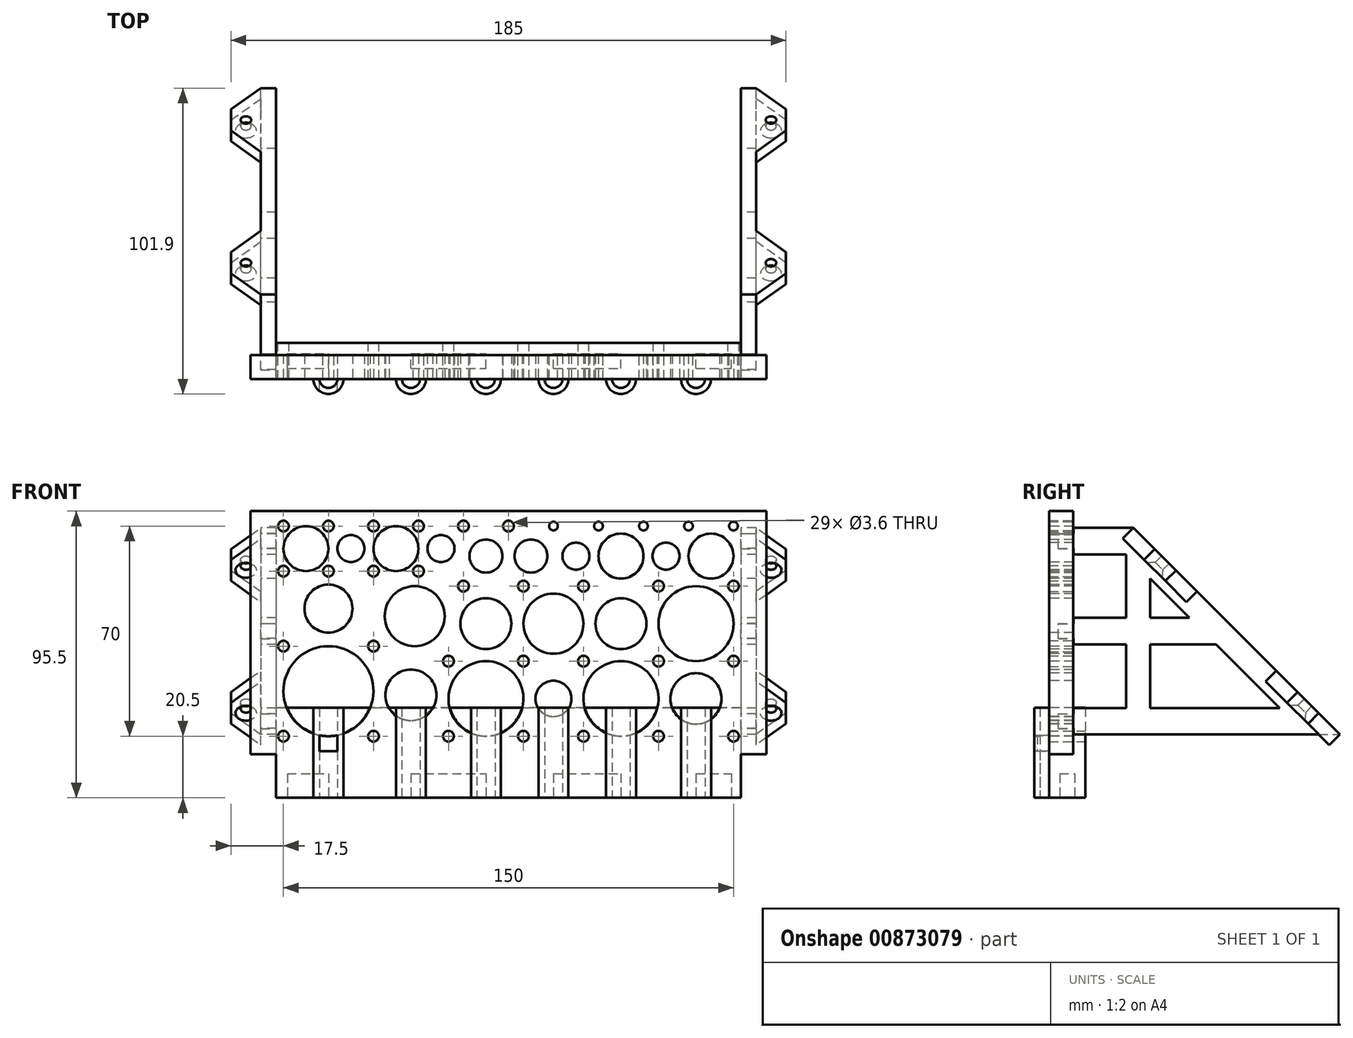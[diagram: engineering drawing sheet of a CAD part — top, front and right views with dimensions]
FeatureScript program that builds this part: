
annotation { "Feature Type Name" : "Feature", "Feature Type Description" : "" }
export const myFeature = defineFeature(function(context is Context, id is Id, definition is map)
    precondition{}
    {
        {
            var Q0;
            Q0=qCreatedBy(makeId("Front.planeOp"),FACE);
            var sketch = newSketch(context, id + "F0", { "sketchPlane" : qUnion([Q0])});
            skCircle(sketch, "E0", {"center": v(-34.8, 20.35) * mm, "radius": 1.8 * mm});
            skCircle(sketch, "E1.0.1.0", {"center": v(-34.8, 50.35) * mm, "radius": 1.8 * mm});
            skCircle(sketch, "E1.1.0.0", {"center": v(-4.8, 20.35) * mm, "radius": 1.8 * mm});
            skCircle(sketch, "E1.1.1.0", {"center": v(-4.8, 50.35) * mm, "radius": 1.8 * mm});
            skLineSegment(sketch, "E1.direction1", {"start": v(-34.8, 20.35) * mm, "end": v(-4.8, 20.35) * mm, "construction": true});
            skLineSegment(sketch, "E1.direction2", {"start": v(-34.8, 20.35) * mm, "end": v(-34.8, 50.35) * mm, "construction": true});
            skCircle(sketch, "E2", {"center": v(20.2, 20.35) * mm, "radius": 1.8 * mm});
            skCircle(sketch, "E3.0.1.0", {"center": v(20.2, 45.35) * mm, "radius": 1.8 * mm});
            skCircle(sketch, "E3.1.0.0", {"center": v(45.2, 20.35) * mm, "radius": 1.8 * mm});
            skCircle(sketch, "E3.1.1.0", {"center": v(45.2, 45.35) * mm, "radius": 1.8 * mm});
            skLineSegment(sketch, "E3.direction1", {"start": v(20.2, 20.35) * mm, "end": v(45.2, 20.35) * mm, "construction": true});
            skLineSegment(sketch, "E3.direction2", {"start": v(20.2, 20.35) * mm, "end": v(20.2, 45.35) * mm, "construction": true});
            skCircle(sketch, "E4", {"center": v(65.2, 20.35) * mm, "radius": 1.8 * mm});
            skCircle(sketch, "E5.0.1.0", {"center": v(65.2, 45.35) * mm, "radius": 1.8 * mm});
            skCircle(sketch, "E5.0.2.0", {"center": v(65.2, 70.35) * mm, "radius": 1.8 * mm});
            skCircle(sketch, "E5.1.0.0", {"center": v(90.2, 20.35) * mm, "radius": 1.8 * mm});
            skCircle(sketch, "E5.1.1.0", {"center": v(90.2, 45.35) * mm, "radius": 1.8 * mm});
            skCircle(sketch, "E5.1.2.0", {"center": v(90.2, 70.35) * mm, "radius": 1.8 * mm});
            skCircle(sketch, "E5.2.0.0", {"center": v(115.2, 20.35) * mm, "radius": 1.8 * mm});
            skCircle(sketch, "E5.2.1.0", {"center": v(115.2, 45.35) * mm, "radius": 1.8 * mm});
            skCircle(sketch, "E5.2.2.0", {"center": v(115.2, 70.35) * mm, "radius": 1.8 * mm});
            skLineSegment(sketch, "E5.direction1", {"start": v(65.2, 20.35) * mm, "end": v(90.2, 20.35) * mm, "construction": true});
            skLineSegment(sketch, "E5.direction2", {"start": v(65.2, 20.35) * mm, "end": v(65.2, 45.35) * mm, "construction": true});
            skCircle(sketch, "E6", {"center": v(-34.8, 90.35) * mm, "radius": 1.8 * mm});
            skCircle(sketch, "E7.1.0.0", {"center": v(-19.8, 90.35) * mm, "radius": 1.8 * mm});
            skCircle(sketch, "E7.2.0.0", {"center": v(-4.8, 90.35) * mm, "radius": 1.8 * mm});
            skCircle(sketch, "E7.3.0.0", {"center": v(10.2, 90.35) * mm, "radius": 1.8 * mm});
            skCircle(sketch, "E7.4.0.0", {"center": v(25.2, 90.35) * mm, "radius": 1.8 * mm});
            skCircle(sketch, "E7.5.0.0", {"center": v(40.2, 90.35) * mm, "radius": 1.8 * mm});
            skLineSegment(sketch, "E7.direction1", {"start": v(-34.8, 90.35) * mm, "end": v(-19.8, 90.35) * mm, "construction": true});
            skCircle(sketch, "E8.0.6.0", {"center": v(55.2, 90.35) * mm, "radius": 1.45 * mm});
            skCircle(sketch, "E8.0.7.0", {"center": v(70.2, 90.35) * mm, "radius": 1.45 * mm});
            skCircle(sketch, "E8.0.8.0", {"center": v(85.2, 90.35) * mm, "radius": 1.45 * mm});
            skCircle(sketch, "E8.0.9.0", {"center": v(100.2, 90.35) * mm, "radius": 1.45 * mm});
            skCircle(sketch, "E9.0.10.0", {"center": v(115.2, 90.35) * mm, "radius": 1.45 * mm});
            skCircle(sketch, "E10.1.0.0", {"center": v(45.2, 70.35) * mm, "radius": 1.8 * mm});
            skCircle(sketch, "E10.2.0.0", {"center": v(25.2, 70.35) * mm, "radius": 1.8 * mm});
            skLineSegment(sketch, "E10.direction1", {"start": v(65.2, 70.35) * mm, "end": v(45.2, 70.35) * mm, "construction": true});
            skLineSegment(sketch, "E11", {"start": v(-39.8, 95.35) * mm, "end": v(-39.8, 15.35) * mm, "construction": true});
            skLineSegment(sketch, "E12", {"start": v(120.2, 95.35) * mm, "end": v(120.2, 15.35) * mm, "construction": true});
            skLineSegment(sketch, "E13", {"start": v(-39.8, 95.35) * mm, "end": v(120.2, 95.35) * mm});
            skLineSegment(sketch, "E14", {"start": v(120.2, 15.35) * mm, "end": v(-39.8, 15.35) * mm});
            skLineSegment(sketch, "E15", {"start": v(-39.8, 95.35) * mm, "end": v(-45.8, 95.35) * mm});
            skLineSegment(sketch, "E16", {"start": v(-39.8, 15.35) * mm, "end": v(-39.8, 15.35) * mm});
            skLineSegment(sketch, "E17", {"start": v(-39.8, 15.35) * mm, "end": v(-45.8, 15.35) * mm});
            skLineSegment(sketch, "E18", {"start": v(-45.8, 15.35) * mm, "end": v(-45.8, 95.35) * mm});
            skLineSegment(sketch, "E19", {"start": v(120.2, 95.35) * mm, "end": v(126.2, 95.35) * mm});
            skLineSegment(sketch, "E20", {"start": v(126.2, 95.35) * mm, "end": v(126.2, 15.35) * mm});
            skLineSegment(sketch, "E21", {"start": v(126.2, 15.35) * mm, "end": v(120.2, 15.35) * mm});
            skCircle(sketch, "E22", {"center": v(-34.8, 75.35) * mm, "radius": 1.8 * mm});
            skCircle(sketch, "E23.1.0.0", {"center": v(-19.8, 75.35) * mm, "radius": 1.8 * mm});
            skCircle(sketch, "E23.2.0.0", {"center": v(-4.8, 75.35) * mm, "radius": 1.8 * mm});
            skCircle(sketch, "E23.3.0.0", {"center": v(10.2, 75.35) * mm, "radius": 1.8 * mm});
            skLineSegment(sketch, "E23.direction1", {"start": v(-34.8, 75.35) * mm, "end": v(-19.8, 75.35) * mm, "construction": true});
            skSolve(sketch);
        }
        {
            var Q0;
            Q0=makeQuery(id+"F0.imprint","IMPRINT",FACE,{"disambiguationData":[TD([[makeQuery(id+"F0.imprint","IMPRINT",EDGE,{"derivedFrom":sQuery(id+"F0.wireOp",EDGE,"E0")}),-1.0]])]});
            extrude(context, id + "F1", {"entities" : qUnion([Q0]), "depth" : 8 * mm, "offsetDistance" : 25 * mm});
        }
        {
            var Q0;
            Q0=makeQuery(id+"F1.opExtrude","CAP_FACE",FACE,{"disambiguationData":[OSD([sQuery(id+"F0.wireOp",EDGE,"E0"),sQuery(id+"F0.wireOp",EDGE,"E1.0.1.0"),sQuery(id+"F0.wireOp",EDGE,"E1.1.0.0"),sQuery(id+"F0.wireOp",EDGE,"E1.1.1.0"),sQuery(id+"F0.wireOp",EDGE,"E2"),sQuery(id+"F0.wireOp",EDGE,"E3.0.1.0"),sQuery(id+"F0.wireOp",EDGE,"E3.1.0.0"),sQuery(id+"F0.wireOp",EDGE,"E3.1.1.0"),sQuery(id+"F0.wireOp",EDGE,"E4"),sQuery(id+"F0.wireOp",EDGE,"E5.0.1.0"),sQuery(id+"F0.wireOp",EDGE,"E5.0.2.0"),sQuery(id+"F0.wireOp",EDGE,"E5.1.0.0"),sQuery(id+"F0.wireOp",EDGE,"E5.1.1.0"),sQuery(id+"F0.wireOp",EDGE,"E5.1.2.0"),sQuery(id+"F0.wireOp",EDGE,"E5.2.0.0"),sQuery(id+"F0.wireOp",EDGE,"E5.2.1.0"),sQuery(id+"F0.wireOp",EDGE,"E5.2.2.0"),sQuery(id+"F0.wireOp",EDGE,"E6"),sQuery(id+"F0.wireOp",EDGE,"E7.1.0.0"),sQuery(id+"F0.wireOp",EDGE,"E7.2.0.0"),sQuery(id+"F0.wireOp",EDGE,"E7.3.0.0"),sQuery(id+"F0.wireOp",EDGE,"E7.4.0.0"),sQuery(id+"F0.wireOp",EDGE,"E7.5.0.0"),sQuery(id+"F0.wireOp",EDGE,"E8.0.6.0"),sQuery(id+"F0.wireOp",EDGE,"E8.0.7.0"),sQuery(id+"F0.wireOp",EDGE,"E8.0.8.0"),sQuery(id+"F0.wireOp",EDGE,"E8.0.9.0"),sQuery(id+"F0.wireOp",EDGE,"E9.0.10.0"),sQuery(id+"F0.wireOp",EDGE,"E10.1.0.0"),sQuery(id+"F0.wireOp",EDGE,"E10.2.0.0"),sQuery(id+"F0.wireOp",EDGE,"E13"),sQuery(id+"F0.wireOp",EDGE,"E14"),sQuery(id+"F0.wireOp",EDGE,"E15"),sQuery(id+"F0.wireOp",EDGE,"E17"),sQuery(id+"F0.wireOp",EDGE,"E18"),sQuery(id+"F0.wireOp",EDGE,"E19"),sQuery(id+"F0.wireOp",EDGE,"E20"),sQuery(id+"F0.wireOp",EDGE,"E21"),sQuery(id+"F0.wireOp",EDGE,"E22"),sQuery(id+"F0.wireOp",EDGE,"E23.1.0.0"),sQuery(id+"F0.wireOp",EDGE,"E23.2.0.0"),sQuery(id+"F0.wireOp",EDGE,"E23.3.0.0")])],"isStart":false});
            var sketch = newSketch(context, id + "F2", { "sketchPlane" : qUnion([Q0])});
            skLineSegment(sketch, "E24.0", {"start": v(126.2, 95.35) * mm, "end": v(126.2, 15.35) * mm});
            skLineSegment(sketch, "E24.1", {"start": v(-45.8, 95.35) * mm, "end": v(126.2, 95.35) * mm});
            skLineSegment(sketch, "E24.2", {"start": v(126.2, 15.35) * mm, "end": v(-45.8, 15.35) * mm});
            skLineSegment(sketch, "E24.3", {"start": v(-45.8, 15.35) * mm, "end": v(-45.8, 95.35) * mm});
            skLineSegment(sketch, "E25", {"start": v(-34.8, 50.35) * mm, "end": v(-4.8, 50.35) * mm, "construction": true});
            skLineSegment(sketch, "E26", {"start": v(-4.8, 50.35) * mm, "end": v(-4.8, 20.35) * mm, "construction": true});
            skLineSegment(sketch, "E27", {"start": v(-4.8, 20.35) * mm, "end": v(-34.8, 20.35) * mm, "construction": true});
            skLineSegment(sketch, "E28", {"start": v(-34.8, 20.35) * mm, "end": v(-34.8, 50.35) * mm, "construction": true});
            skLineSegment(sketch, "E29", {"start": v(20.2, 45.35) * mm, "end": v(45.2, 45.35) * mm, "construction": true});
            skLineSegment(sketch, "E30", {"start": v(45.2, 45.35) * mm, "end": v(45.2, 20.35) * mm, "construction": true});
            skLineSegment(sketch, "E31", {"start": v(45.2, 20.35) * mm, "end": v(20.2, 20.35) * mm, "construction": true});
            skLineSegment(sketch, "E32", {"start": v(20.2, 20.35) * mm, "end": v(20.2, 45.35) * mm, "construction": true});
            skLineSegment(sketch, "E33", {"start": v(45.2, 45.35) * mm, "end": v(115.2, 45.35) * mm, "construction": true});
            skLineSegment(sketch, "E34", {"start": v(45.2, 20.35) * mm, "end": v(115.2, 20.35) * mm, "construction": true});
            skLineSegment(sketch, "E35", {"start": v(65.2, 45.35) * mm, "end": v(65.2, 20.35) * mm, "construction": true});
            skLineSegment(sketch, "E36", {"start": v(90.2, 45.35) * mm, "end": v(90.2, 20.35) * mm, "construction": true});
            skLineSegment(sketch, "E37", {"start": v(115.2, 45.35) * mm, "end": v(115.2, 20.35) * mm, "construction": true});
            skCircle(sketch, "E38", {"center": v(-19.8, 35.35) * mm, "radius": 15 * mm});
            skPoint(sketch, "E38.centerSnap0", {"position": v(-19.8, 50.35) * mm});
            skPoint(sketch, "E38.centerSnap1", {"position": v(-34.8, 35.35) * mm});
            skCircle(sketch, "E39", {"center": v(32.7, 32.85) * mm, "radius": 12.5 * mm});
            skPoint(sketch, "E39.centerSnap0", {"position": v(32.7, 45.35) * mm});
            skPoint(sketch, "E39.centerSnap1", {"position": v(20.2, 32.85) * mm});
            skPoint(sketch, "E40", {"position": v(55.2, 32.85) * mm});
            skPoint(sketch, "E40.positionSnap0", {"position": v(65.2, 32.85) * mm});
            skPoint(sketch, "E41", {"position": v(77.7, 32.85) * mm});
            skPoint(sketch, "E42", {"position": v(102.7, 32.85) * mm});
            skCircle(sketch, "E43", {"center": v(55.2, 32.85) * mm, "radius": 6 * mm});
            skCircle(sketch, "E44", {"center": v(77.7, 32.85) * mm, "radius": 12.5 * mm});
            skCircle(sketch, "E45", {"center": v(102.7, 32.85) * mm, "radius": 8.5 * mm});
            skLineSegment(sketch, "E46", {"start": v(-19.8, 35.35) * mm, "end": v(32.7, 32.85) * mm, "construction": true});
            skPoint(sketch, "E47", {"position": v(7.7, 34.04) * mm});
            skCircle(sketch, "E48", {"center": v(7.7, 34.04) * mm, "radius": 8.5 * mm});
            skLineSegment(sketch, "E49", {"start": v(115.2, 90.35) * mm, "end": v(100.2, 90.35) * mm, "construction": true});
            skLineSegment(sketch, "E50", {"start": v(100.2, 90.35) * mm, "end": v(85.2, 90.35) * mm, "construction": true});
            skLineSegment(sketch, "E51", {"start": v(85.2, 90.35) * mm, "end": v(70.2, 90.35) * mm, "construction": true});
            skLineSegment(sketch, "E52", {"start": v(70.2, 90.35) * mm, "end": v(55.2, 90.35) * mm, "construction": true});
            skLineSegment(sketch, "E53", {"start": v(55.2, 90.35) * mm, "end": v(40.2, 90.35) * mm, "construction": true});
            skLineSegment(sketch, "E54", {"start": v(40.2, 90.35) * mm, "end": v(25.2, 90.35) * mm, "construction": true});
            skLineSegment(sketch, "E55", {"start": v(25.2, 90.35) * mm, "end": v(10.2, 90.35) * mm, "construction": true});
            skLineSegment(sketch, "E56", {"start": v(10.2, 90.35) * mm, "end": v(-4.8, 90.35) * mm, "construction": true});
            skLineSegment(sketch, "E57", {"start": v(-4.8, 90.35) * mm, "end": v(-19.8, 90.35) * mm, "construction": true});
            skLineSegment(sketch, "E58", {"start": v(-19.8, 90.35) * mm, "end": v(-34.8, 90.35) * mm, "construction": true});
            skLineSegment(sketch, "E59", {"start": v(-34.8, 90.35) * mm, "end": v(-34.8, 75.35) * mm, "construction": true});
            skCircle(sketch, "E60", {"center": v(-27.3, 82.85) * mm, "radius": 7.5 * mm});
            skPoint(sketch, "E60.centerSnap0", {"position": v(-27.3, 90.35) * mm});
            skPoint(sketch, "E60.centerSnap1", {"position": v(-34.8, 82.85) * mm});
            skCircle(sketch, "E61", {"center": v(2.7, 82.85) * mm, "radius": 7.5 * mm});
            skPoint(sketch, "E61.centerSnap0", {"position": v(2.7, 90.35) * mm});
            skCircle(sketch, "E62", {"center": v(-12.3, 82.85) * mm, "radius": 4.5 * mm});
            skPoint(sketch, "E62.centerSnap0", {"position": v(-12.3, 90.35) * mm});
            skCircle(sketch, "E63", {"center": v(17.7, 82.85) * mm, "radius": 4.5 * mm});
            skPoint(sketch, "E63.centerSnap0", {"position": v(17.7, 90.35) * mm});
            skLineSegment(sketch, "E64", {"start": v(-34.8, 75.35) * mm, "end": v(-34.8, 50.35) * mm, "construction": true});
            skLineSegment(sketch, "E65", {"start": v(-34.8, 62.85) * mm, "end": v(-4.8, 62.85) * mm, "construction": true});
            skLineSegment(sketch, "E66", {"start": v(20.2, 45.35) * mm, "end": v(25.2, 70.35) * mm, "construction": true});
            skLineSegment(sketch, "E67", {"start": v(22.7, 57.85) * mm, "end": v(-4.8, 62.85) * mm, "construction": true});
            skCircle(sketch, "E68", {"center": v(-19.8, 62.85) * mm, "radius": 8 * mm});
            skCircle(sketch, "E69", {"center": v(8.95, 60.35) * mm, "radius": 10 * mm});
            skLineSegment(sketch, "E70", {"start": v(25.2, 70.35) * mm, "end": v(45.2, 70.35) * mm, "construction": true});
            skLineSegment(sketch, "E71", {"start": v(45.2, 70.35) * mm, "end": v(65.2, 70.35) * mm, "construction": true});
            skLineSegment(sketch, "E72", {"start": v(65.2, 70.35) * mm, "end": v(90.2, 70.35) * mm, "construction": true});
            skLineSegment(sketch, "E73", {"start": v(90.2, 70.35) * mm, "end": v(115.2, 70.35) * mm, "construction": true});
            skLineSegment(sketch, "E74", {"start": v(115.2, 70.35) * mm, "end": v(115.2, 45.35) * mm, "construction": true});
            skLineSegment(sketch, "E75", {"start": v(115.2, 57.85) * mm, "end": v(22.7, 57.85) * mm, "construction": true});
            skCircle(sketch, "E76", {"center": v(102.7, 57.85) * mm, "radius": 12.5 * mm});
            skPoint(sketch, "E76.centerSnap0", {"position": v(102.7, 70.35) * mm});
            skCircle(sketch, "E77", {"center": v(77.7, 57.85) * mm, "radius": 8.5 * mm});
            skPoint(sketch, "E77.centerSnap0", {"position": v(77.7, 70.35) * mm});
            skCircle(sketch, "E78", {"center": v(55.2, 57.85) * mm, "radius": 10 * mm});
            skPoint(sketch, "E78.centerSnap0", {"position": v(55.2, 70.35) * mm});
            skCircle(sketch, "E79", {"center": v(32.68, 57.85) * mm, "radius": 8.5 * mm});
            skLineSegment(sketch, "E80", {"start": v(115.2, 90.35) * mm, "end": v(115.2, 70.35) * mm, "construction": true});
            skLineSegment(sketch, "E81", {"start": v(115.2, 80.35) * mm, "end": v(32.7, 80.35) * mm, "construction": true});
            skPoint(sketch, "E81.endSnap0", {"position": v(32.7, 90.35) * mm});
            skCircle(sketch, "E82", {"center": v(107.7, 80.35) * mm, "radius": 7.5 * mm});
            skPoint(sketch, "E82.centerSnap0", {"position": v(107.7, 90.35) * mm});
            skCircle(sketch, "E83", {"center": v(92.7, 80.35) * mm, "radius": 4.5 * mm});
            skPoint(sketch, "E83.centerSnap0", {"position": v(92.7, 90.35) * mm});
            skCircle(sketch, "E84", {"center": v(77.7, 80.35) * mm, "radius": 7.5 * mm});
            skPoint(sketch, "E84.centerSnap0", {"position": v(77.7, 90.35) * mm});
            skCircle(sketch, "E85", {"center": v(62.7, 80.35) * mm, "radius": 4.5 * mm});
            skPoint(sketch, "E85.centerSnap0", {"position": v(62.7, 90.35) * mm});
            skCircle(sketch, "E86", {"center": v(47.7, 80.35) * mm, "radius": 5.5 * mm});
            skPoint(sketch, "E86.centerSnap0", {"position": v(47.7, 90.35) * mm});
            skCircle(sketch, "E87", {"center": v(32.7, 80.35) * mm, "radius": 5.5 * mm});
            skSolve(sketch);
        }
        {
            var Q0;
            Q0=makeQuery(id+"F2.imprint","IMPRINT",FACE,{"disambiguationData":[TD([[makeQuery(id+"F2.imprint","IMPRINT",EDGE,{"derivedFrom":sQuery(id+"F2.wireOp",EDGE,"E45")}),1.0]])]});
            var Q1;
            Q1=makeQuery(id+"F2.imprint","IMPRINT",FACE,{"disambiguationData":[TD([[makeQuery(id+"F2.imprint","IMPRINT",EDGE,{"derivedFrom":sQuery(id+"F2.wireOp",EDGE,"E44")}),1.0]])]});
            var Q2;
            Q2=makeQuery(id+"F2.imprint","IMPRINT",FACE,{"disambiguationData":[TD([[makeQuery(id+"F2.imprint","IMPRINT",EDGE,{"derivedFrom":sQuery(id+"F2.wireOp",EDGE,"E43")}),1.0]])]});
            var Q3;
            Q3=makeQuery(id+"F2.imprint","IMPRINT",FACE,{"disambiguationData":[TD([[makeQuery(id+"F2.imprint","IMPRINT",EDGE,{"derivedFrom":sQuery(id+"F2.wireOp",EDGE,"E39")}),1.0]])]});
            var Q4;
            Q4=makeQuery(id+"F2.imprint","IMPRINT",FACE,{"disambiguationData":[TD([[makeQuery(id+"F2.imprint","IMPRINT",EDGE,{"derivedFrom":sQuery(id+"F2.wireOp",EDGE,"E48")}),1.0]])]});
            var Q5;
            Q5=makeQuery(id+"F2.imprint","IMPRINT",FACE,{"disambiguationData":[TD([[makeQuery(id+"F2.imprint","IMPRINT",EDGE,{"derivedFrom":sQuery(id+"F2.wireOp",EDGE,"E38")}),1.0]])]});
            var Q6;
            Q6=makeQuery(id+"F2.imprint","IMPRINT",FACE,{"disambiguationData":[TD([[makeQuery(id+"F2.imprint","IMPRINT",EDGE,{"derivedFrom":sQuery(id+"F2.wireOp",EDGE,"E68")}),1.0]])]});
            var Q7;
            Q7=makeQuery(id+"F2.imprint","IMPRINT",FACE,{"disambiguationData":[TD([[makeQuery(id+"F2.imprint","IMPRINT",EDGE,{"derivedFrom":sQuery(id+"F2.wireOp",EDGE,"E60")}),1.0]])]});
            var Q8;
            Q8=makeQuery(id+"F2.imprint","IMPRINT",FACE,{"disambiguationData":[TD([[makeQuery(id+"F2.imprint","IMPRINT",EDGE,{"derivedFrom":sQuery(id+"F2.wireOp",EDGE,"E62")}),1.0]])]});
            var Q9;
            Q9=makeQuery(id+"F2.imprint","IMPRINT",FACE,{"disambiguationData":[TD([[makeQuery(id+"F2.imprint","IMPRINT",EDGE,{"derivedFrom":sQuery(id+"F2.wireOp",EDGE,"E61")}),1.0]])]});
            var Q10;
            Q10=makeQuery(id+"F2.imprint","IMPRINT",FACE,{"disambiguationData":[TD([[makeQuery(id+"F2.imprint","IMPRINT",EDGE,{"derivedFrom":sQuery(id+"F2.wireOp",EDGE,"E63")}),1.0]])]});
            var Q11;
            Q11=makeQuery(id+"F2.imprint","IMPRINT",FACE,{"disambiguationData":[TD([[makeQuery(id+"F2.imprint","IMPRINT",EDGE,{"derivedFrom":sQuery(id+"F2.wireOp",EDGE,"E69")}),1.0]])]});
            var Q12;
            Q12=makeQuery(id+"F2.imprint","IMPRINT",FACE,{"disambiguationData":[TD([[makeQuery(id+"F2.imprint","IMPRINT",EDGE,{"derivedFrom":sQuery(id+"F2.wireOp",EDGE,"E79")}),1.0]])]});
            var Q13;
            Q13=makeQuery(id+"F2.imprint","IMPRINT",FACE,{"disambiguationData":[TD([[makeQuery(id+"F2.imprint","IMPRINT",EDGE,{"derivedFrom":sQuery(id+"F2.wireOp",EDGE,"E78")}),1.0]])]});
            var Q14;
            Q14=makeQuery(id+"F2.imprint","IMPRINT",FACE,{"disambiguationData":[TD([[makeQuery(id+"F2.imprint","IMPRINT",EDGE,{"derivedFrom":sQuery(id+"F2.wireOp",EDGE,"E77")}),1.0]])]});
            var Q15;
            Q15=makeQuery(id+"F2.imprint","IMPRINT",FACE,{"disambiguationData":[TD([[makeQuery(id+"F2.imprint","IMPRINT",EDGE,{"derivedFrom":sQuery(id+"F2.wireOp",EDGE,"E76")}),1.0]])]});
            var Q16;
            Q16=makeQuery(id+"F2.imprint","IMPRINT",FACE,{"disambiguationData":[TD([[makeQuery(id+"F2.imprint","IMPRINT",EDGE,{"derivedFrom":sQuery(id+"F2.wireOp",EDGE,"E87")}),1.0]])]});
            var Q17;
            Q17=makeQuery(id+"F2.imprint","IMPRINT",FACE,{"disambiguationData":[TD([[makeQuery(id+"F2.imprint","IMPRINT",EDGE,{"derivedFrom":sQuery(id+"F2.wireOp",EDGE,"E86")}),1.0]])]});
            var Q18;
            Q18=makeQuery(id+"F2.imprint","IMPRINT",FACE,{"disambiguationData":[TD([[makeQuery(id+"F2.imprint","IMPRINT",EDGE,{"derivedFrom":sQuery(id+"F2.wireOp",EDGE,"E85")}),1.0]])]});
            var Q19;
            Q19=makeQuery(id+"F2.imprint","IMPRINT",FACE,{"disambiguationData":[TD([[makeQuery(id+"F2.imprint","IMPRINT",EDGE,{"derivedFrom":sQuery(id+"F2.wireOp",EDGE,"E84")}),1.0]])]});
            var Q20;
            Q20=makeQuery(id+"F2.imprint","IMPRINT",FACE,{"disambiguationData":[TD([[makeQuery(id+"F2.imprint","IMPRINT",EDGE,{"derivedFrom":sQuery(id+"F2.wireOp",EDGE,"E83")}),1.0]])]});
            var Q21;
            Q21=makeQuery(id+"F2.imprint","IMPRINT",FACE,{"disambiguationData":[TD([[makeQuery(id+"F2.imprint","IMPRINT",EDGE,{"derivedFrom":sQuery(id+"F2.wireOp",EDGE,"E82")}),1.0]])]});
            extrude(context, id + "F3", {"entities" : qUnion([Q0, Q1, Q2, Q3, Q4, Q5, Q6, Q7, Q8, Q9, Q10, Q11, Q12, Q13, Q14, Q15, Q16, Q17, Q18, Q19, Q20, Q21]), "operationType" : NewBodyOperationType.REMOVE, "oppositeDirection" : true, "depth" : 8 * mm, "offsetDistance" : 25 * mm});
        }
        {
            var Q0;
            Q0=makeQuery(id+"F1.opExtrude","CAP_FACE",FACE,{"disambiguationData":[OSD([sQuery(id+"F0.wireOp",EDGE,"E0"),sQuery(id+"F0.wireOp",EDGE,"E1.0.1.0"),sQuery(id+"F0.wireOp",EDGE,"E1.1.0.0"),sQuery(id+"F0.wireOp",EDGE,"E1.1.1.0"),sQuery(id+"F0.wireOp",EDGE,"E2"),sQuery(id+"F0.wireOp",EDGE,"E3.0.1.0"),sQuery(id+"F0.wireOp",EDGE,"E3.1.0.0"),sQuery(id+"F0.wireOp",EDGE,"E3.1.1.0"),sQuery(id+"F0.wireOp",EDGE,"E4"),sQuery(id+"F0.wireOp",EDGE,"E5.0.1.0"),sQuery(id+"F0.wireOp",EDGE,"E5.0.2.0"),sQuery(id+"F0.wireOp",EDGE,"E5.1.0.0"),sQuery(id+"F0.wireOp",EDGE,"E5.1.1.0"),sQuery(id+"F0.wireOp",EDGE,"E5.1.2.0"),sQuery(id+"F0.wireOp",EDGE,"E5.2.0.0"),sQuery(id+"F0.wireOp",EDGE,"E5.2.1.0"),sQuery(id+"F0.wireOp",EDGE,"E5.2.2.0"),sQuery(id+"F0.wireOp",EDGE,"E6"),sQuery(id+"F0.wireOp",EDGE,"E7.1.0.0"),sQuery(id+"F0.wireOp",EDGE,"E7.2.0.0"),sQuery(id+"F0.wireOp",EDGE,"E7.3.0.0"),sQuery(id+"F0.wireOp",EDGE,"E7.4.0.0"),sQuery(id+"F0.wireOp",EDGE,"E7.5.0.0"),sQuery(id+"F0.wireOp",EDGE,"E8.0.6.0"),sQuery(id+"F0.wireOp",EDGE,"E8.0.7.0"),sQuery(id+"F0.wireOp",EDGE,"E8.0.8.0"),sQuery(id+"F0.wireOp",EDGE,"E8.0.9.0"),sQuery(id+"F0.wireOp",EDGE,"E9.0.10.0"),sQuery(id+"F0.wireOp",EDGE,"E10.1.0.0"),sQuery(id+"F0.wireOp",EDGE,"E10.2.0.0"),sQuery(id+"F0.wireOp",EDGE,"E13"),sQuery(id+"F0.wireOp",EDGE,"E14"),sQuery(id+"F0.wireOp",EDGE,"E15"),sQuery(id+"F0.wireOp",EDGE,"E17"),sQuery(id+"F0.wireOp",EDGE,"E18"),sQuery(id+"F0.wireOp",EDGE,"E19"),sQuery(id+"F0.wireOp",EDGE,"E20"),sQuery(id+"F0.wireOp",EDGE,"E21"),sQuery(id+"F0.wireOp",EDGE,"E22"),sQuery(id+"F0.wireOp",EDGE,"E23.1.0.0"),sQuery(id+"F0.wireOp",EDGE,"E23.2.0.0"),sQuery(id+"F0.wireOp",EDGE,"E23.3.0.0")])],"isStart":true});
            var sketch = newSketch(context, id + "F4", { "sketchPlane" : qUnion([Q0])});
            skLineSegment(sketch, "E88.0", {"start": v(45.8, 95.35) * mm, "end": v(-126.2, 95.35) * mm});
            skLineSegment(sketch, "E88.1", {"start": v(45.8, 15.35) * mm, "end": v(45.8, 95.35) * mm});
            skLineSegment(sketch, "E88.2", {"start": v(-126.2, 15.35) * mm, "end": v(45.8, 15.35) * mm});
            skLineSegment(sketch, "E88.3", {"start": v(-126.2, 95.35) * mm, "end": v(-126.2, 15.35) * mm});
            skLineSegment(sketch, "E89.bottom", {"start": v(-117.7, 82.85) * mm, "end": v(-122.7, 82.85) * mm});
            skLineSegment(sketch, "E89.top", {"start": v(-117.7, 87.85) * mm, "end": v(-122.7, 87.85) * mm});
            skLineSegment(sketch, "E89.left", {"start": v(-117.7, 82.85) * mm, "end": v(-117.7, 87.85) * mm});
            skLineSegment(sketch, "E89.right", {"start": v(-122.7, 82.85) * mm, "end": v(-122.7, 87.85) * mm});
            skPoint(sketch, "E89.middle", {"position": v(-120.2, 85.35) * mm});
            skLineSegment(sketch, "E90.bottom", {"start": v(-122.7, 52.85) * mm, "end": v(-117.7, 52.85) * mm});
            skLineSegment(sketch, "E90.top", {"start": v(-122.7, 57.85) * mm, "end": v(-117.7, 57.85) * mm});
            skLineSegment(sketch, "E90.left", {"start": v(-122.7, 52.85) * mm, "end": v(-122.7, 57.85) * mm});
            skLineSegment(sketch, "E90.right", {"start": v(-117.7, 52.85) * mm, "end": v(-117.7, 57.85) * mm});
            skPoint(sketch, "E90.middle", {"position": v(-120.2, 55.35) * mm});
            skLineSegment(sketch, "E91.bottom", {"start": v(-122.7, 22.85) * mm, "end": v(-117.7, 22.85) * mm});
            skLineSegment(sketch, "E91.top", {"start": v(-122.7, 27.85) * mm, "end": v(-117.7, 27.85) * mm});
            skLineSegment(sketch, "E91.left", {"start": v(-122.7, 22.85) * mm, "end": v(-122.7, 27.85) * mm});
            skLineSegment(sketch, "E91.right", {"start": v(-117.7, 22.85) * mm, "end": v(-117.7, 27.85) * mm});
            skPoint(sketch, "E91.middle", {"position": v(-120.2, 25.35) * mm});
            skLineSegment(sketch, "E92", {"start": v(-40.2, 95.35) * mm, "end": v(-40.2, 15.35) * mm, "construction": true});
            skLineSegment(sketch, "E93.MirrorCS", {"start": v(37.3, 87.85) * mm, "end": v(42.3, 87.85) * mm});
            skLineSegment(sketch, "E94.MirrorCS", {"start": v(37.3, 82.85) * mm, "end": v(37.3, 87.85) * mm});
            skLineSegment(sketch, "E95.MirrorCS", {"start": v(37.3, 82.85) * mm, "end": v(42.3, 82.85) * mm});
            skLineSegment(sketch, "E96.MirrorCS", {"start": v(42.3, 82.85) * mm, "end": v(42.3, 87.85) * mm});
            skLineSegment(sketch, "E97.MirrorCS", {"start": v(42.3, 57.85) * mm, "end": v(37.3, 57.85) * mm});
            skLineSegment(sketch, "E98.MirrorCS", {"start": v(37.3, 52.85) * mm, "end": v(37.3, 57.85) * mm});
            skLineSegment(sketch, "E99.MirrorCS", {"start": v(42.3, 52.85) * mm, "end": v(37.3, 52.85) * mm});
            skLineSegment(sketch, "E100.MirrorCS", {"start": v(42.3, 52.85) * mm, "end": v(42.3, 57.85) * mm});
            skLineSegment(sketch, "E101.MirrorCS", {"start": v(42.3, 27.85) * mm, "end": v(37.3, 27.85) * mm});
            skLineSegment(sketch, "E102.MirrorCS", {"start": v(37.3, 22.85) * mm, "end": v(37.3, 27.85) * mm});
            skLineSegment(sketch, "E103.MirrorCS", {"start": v(42.3, 22.85) * mm, "end": v(37.3, 22.85) * mm});
            skLineSegment(sketch, "E104.MirrorCS", {"start": v(42.3, 22.85) * mm, "end": v(42.3, 27.85) * mm});
            skSolve(sketch);
        }
        {
            var Q0;
            Q0=makeQuery(id+"F4.imprint","IMPRINT",FACE,{"disambiguationData":[TD([[makeQuery(id+"F4.imprint","IMPRINT",EDGE,{"derivedFrom":sQuery(id+"F4.wireOp",EDGE,"E89.bottom")}),-1.0]])]});
            var Q1;
            Q1=makeQuery(id+"F4.imprint","IMPRINT",FACE,{"disambiguationData":[TD([[makeQuery(id+"F4.imprint","IMPRINT",EDGE,{"derivedFrom":sQuery(id+"F4.wireOp",EDGE,"E90.bottom")}),1.0]])]});
            var Q2;
            Q2=makeQuery(id+"F4.imprint","IMPRINT",FACE,{"disambiguationData":[TD([[makeQuery(id+"F4.imprint","IMPRINT",EDGE,{"derivedFrom":sQuery(id+"F4.wireOp",EDGE,"E91.bottom")}),1.0]])]});
            var Q3;
            Q3=makeQuery(id+"F4.imprint","IMPRINT",FACE,{"disambiguationData":[TD([[makeQuery(id+"F4.imprint","IMPRINT",EDGE,{"derivedFrom":sQuery(id+"F4.wireOp",EDGE,"E101.MirrorCS")}),1.0]])]});
            var Q4;
            Q4=makeQuery(id+"F4.imprint","IMPRINT",FACE,{"disambiguationData":[TD([[makeQuery(id+"F4.imprint","IMPRINT",EDGE,{"derivedFrom":sQuery(id+"F4.wireOp",EDGE,"E97.MirrorCS")}),1.0]])]});
            var Q5;
            Q5=makeQuery(id+"F4.imprint","IMPRINT",FACE,{"disambiguationData":[TD([[makeQuery(id+"F4.imprint","IMPRINT",EDGE,{"derivedFrom":sQuery(id+"F4.wireOp",EDGE,"E93.MirrorCS")}),-1.0]])]});
            extrude(context, id + "F5", {"entities" : qUnion([Q0, Q1, Q2, Q3, Q4, Q5]), "operationType" : NewBodyOperationType.REMOVE, "oppositeDirection" : true, "depth" : 5 * mm, "offsetDistance" : 25 * mm});
        }
        {
            var Q0;
            Q0=makeQuery(id+"F5.boolean.opBoolean","COPY",FACE,{"derivedFrom":makeQuery(id+"F5.opExtrude","SWEPT_FACE",FACE,{"disambiguationData":[OSD([sQuery(id+"F4.wireOp",EDGE,"E89.left")])]})});
            var sketch = newSketch(context, id + "F6", { "sketchPlane" : qUnion([Q0])});
            skLineSegment(sketch, "E105.0", {"start": v(-4.9, 87.75) * mm, "end": v(0, 87.75) * mm});
            skLineSegment(sketch, "E105.1", {"start": v(-4.9, 82.95) * mm, "end": v(-4.9, 87.75) * mm});
            skLineSegment(sketch, "E105.2", {"start": v(-4.9, 82.95) * mm, "end": v(0, 82.95) * mm});
            skLineSegment(sketch, "E106.0", {"start": v(-4.9, 57.75) * mm, "end": v(0, 57.75) * mm});
            skLineSegment(sketch, "E106.1", {"start": v(-4.9, 52.95) * mm, "end": v(-4.9, 57.75) * mm});
            skLineSegment(sketch, "E106.2", {"start": v(-4.9, 52.95) * mm, "end": v(0, 52.95) * mm});
            skLineSegment(sketch, "E107.0", {"start": v(-4.9, 27.75) * mm, "end": v(0, 27.75) * mm});
            skLineSegment(sketch, "E107.1", {"start": v(-4.9, 22.95) * mm, "end": v(-4.9, 27.75) * mm});
            skLineSegment(sketch, "E107.2", {"start": v(-4.9, 22.95) * mm, "end": v(0, 22.95) * mm});
            skLineSegment(sketch, "E108.0", {"start": v(0.1, 95.35) * mm, "end": v(0.1, 87.75) * mm});
            skLineSegment(sketch, "E109", {"start": v(0, 57.75) * mm, "end": v(0.1, 57.75) * mm});
            skLineSegment(sketch, "E110", {"start": v(0, 52.95) * mm, "end": v(0.1, 52.95) * mm});
            skLineSegment(sketch, "E111.trimOffspring", {"start": v(0.1, 52.95) * mm, "end": v(0.1, 27.75) * mm});
            skLineSegment(sketch, "E112", {"start": v(0.1, 59.75) * mm, "end": v(5.1, 59.75) * mm});
            skLineSegment(sketch, "E113", {"start": v(0.1, 50.95) * mm, "end": v(5.1, 50.95) * mm});
            skLineSegment(sketch, "E114", {"start": v(0, 87.75) * mm, "end": v(0.1, 87.75) * mm});
            skLineSegment(sketch, "E115", {"start": v(0, 82.95) * mm, "end": v(0.1, 82.95) * mm});
            skLineSegment(sketch, "E116.trimOffspring", {"start": v(0.1, 82.95) * mm, "end": v(0.1, 57.75) * mm});
            skLineSegment(sketch, "E117", {"start": v(0.1, 80.95) * mm, "end": v(5.1, 80.95) * mm});
            skLineSegment(sketch, "E118", {"start": v(0.1, 89.75) * mm, "end": v(5.1, 89.75) * mm});
            skLineSegment(sketch, "E119", {"start": v(0, 27.75) * mm, "end": v(0.1, 27.75) * mm});
            skLineSegment(sketch, "E120", {"start": v(0, 22.95) * mm, "end": v(0.1, 22.95) * mm});
            skLineSegment(sketch, "E121.trimOffspring", {"start": v(0.1, 22.95) * mm, "end": v(0.1, 15.35) * mm});
            skLineSegment(sketch, "E122", {"start": v(0.1, 29.75) * mm, "end": v(5.1, 29.75) * mm});
            skLineSegment(sketch, "E123", {"start": v(0.1, 20.95) * mm, "end": v(5.1, 20.95) * mm});
            skLineSegment(sketch, "E124", {"start": v(5.1, 89.75) * mm, "end": v(20.1, 89.75) * mm});
            skLineSegment(sketch, "E125", {"start": v(20.1, 89.75) * mm, "end": v(88.9, 20.95) * mm});
            skLineSegment(sketch, "E126", {"start": v(5.1, 20.95) * mm, "end": v(88.9, 20.95) * mm});
            skLineSegment(sketch, "E127", {"start": v(5.1, 29.75) * mm, "end": v(17.59, 29.75) * mm});
            skLineSegment(sketch, "E128", {"start": v(5.1, 50.95) * mm, "end": v(17.59, 50.95) * mm});
            skLineSegment(sketch, "E129", {"start": v(5.1, 59.75) * mm, "end": v(17.59, 59.75) * mm});
            skLineSegment(sketch, "E130", {"start": v(5.1, 80.95) * mm, "end": v(17.59, 80.95) * mm});
            skLineSegment(sketch, "E131.0", {"start": v(25.59, 72.95) * mm, "end": v(38.79, 59.75) * mm});
            skLineSegment(sketch, "E132.trimOffspring", {"start": v(47.59, 50.95) * mm, "end": v(68.79, 29.75) * mm});
            skLineSegment(sketch, "E133", {"start": v(17.59, 80.95) * mm, "end": v(17.59, 59.75) * mm});
            skLineSegment(sketch, "E134", {"start": v(25.59, 29.75) * mm, "end": v(25.59, 50.95) * mm});
            skLineSegment(sketch, "E135.trimOffspring", {"start": v(25.59, 59.75) * mm, "end": v(38.79, 59.75) * mm});
            skLineSegment(sketch, "E136.trimOffspring", {"start": v(25.59, 59.75) * mm, "end": v(25.59, 72.95) * mm});
            skLineSegment(sketch, "E137.trimOffspring", {"start": v(17.59, 50.95) * mm, "end": v(17.59, 29.75) * mm});
            skLineSegment(sketch, "E138.trimOffspring", {"start": v(25.59, 50.95) * mm, "end": v(47.59, 50.95) * mm});
            skLineSegment(sketch, "E139.trimOffspring", {"start": v(25.59, 29.75) * mm, "end": v(68.79, 29.75) * mm});
            skSolve(sketch);
        }
        {
            var Q0;
            Q0=makeQuery(id+"F6.imprint","IMPRINT",FACE,{"disambiguationData":[TD([[makeQuery(id+"F6.imprint","IMPRINT",EDGE,{"derivedFrom":sQuery(id+"F6.wireOp",EDGE,"E106.0")}),-1.0]])]});
            var Q1;
            {var subQ0=sQuery(id+"F6.wireOp",EDGE,"E105.0");Q1=makeQuery(id+"F6.imprint","IMPRINT",FACE,{"disambiguationData":[TD([[makeQuery(id+"F6.imprint","IMPRINT",EDGE,{"derivedFrom":subQ0}),-1.0]])]});}
            extrude(context, id + "F7", {"entities" : qUnion([Q0, Q1]), "depth" : 5 * mm, "offsetDistance" : 25 * mm});
        }
        {
            var Q0;
            Q0=makeQuery(id+"F7.opExtrude","SWEPT_BODY",BODY,{"disambiguationData":[OSD([sQuery(id+"F6.wireOp",EDGE,"E105.0"),sQuery(id+"F6.wireOp",EDGE,"E105.1"),sQuery(id+"F6.wireOp",EDGE,"E105.2"),sQuery(id+"F6.wireOp",EDGE,"E106.0"),sQuery(id+"F6.wireOp",EDGE,"E106.1"),sQuery(id+"F6.wireOp",EDGE,"E106.2"),sQuery(id+"F6.wireOp",EDGE,"E107.0"),sQuery(id+"F6.wireOp",EDGE,"E107.1"),sQuery(id+"F6.wireOp",EDGE,"E107.2"),sQuery(id+"F6.wireOp",EDGE,"E108.0"),sQuery(id+"F6.wireOp",EDGE,"E109"),sQuery(id+"F6.wireOp",EDGE,"E110"),sQuery(id+"F6.wireOp",EDGE,"E111.trimOffspring"),sQuery(id+"F6.wireOp",EDGE,"E112"),sQuery(id+"F6.wireOp",EDGE,"E113"),sQuery(id+"F6.wireOp",EDGE,"E114"),sQuery(id+"F6.wireOp",EDGE,"E115"),sQuery(id+"F6.wireOp",EDGE,"E116.trimOffspring"),sQuery(id+"F6.wireOp",EDGE,"E117"),sQuery(id+"F6.wireOp",EDGE,"E118"),sQuery(id+"F6.wireOp",EDGE,"E119"),sQuery(id+"F6.wireOp",EDGE,"E120"),sQuery(id+"F6.wireOp",EDGE,"E121.trimOffspring"),sQuery(id+"F6.wireOp",EDGE,"E122"),sQuery(id+"F6.wireOp",EDGE,"E123"),sQuery(id+"F6.wireOp",EDGE,"E124"),sQuery(id+"F6.wireOp",EDGE,"E125"),sQuery(id+"F6.wireOp",EDGE,"E126"),sQuery(id+"F6.wireOp",EDGE,"E127"),sQuery(id+"F6.wireOp",EDGE,"E128"),sQuery(id+"F6.wireOp",EDGE,"E129"),sQuery(id+"F6.wireOp",EDGE,"E130"),sQuery(id+"F6.wireOp",EDGE,"E131.0"),sQuery(id+"F6.wireOp",EDGE,"E132.trimOffspring"),sQuery(id+"F6.wireOp",EDGE,"E133"),sQuery(id+"F6.wireOp",EDGE,"E134"),sQuery(id+"F6.wireOp",EDGE,"E135.trimOffspring"),sQuery(id+"F6.wireOp",EDGE,"E136.trimOffspring"),sQuery(id+"F6.wireOp",EDGE,"E137.trimOffspring"),sQuery(id+"F6.wireOp",EDGE,"E138.trimOffspring"),sQuery(id+"F6.wireOp",EDGE,"E139.trimOffspring")])]});
            transform(context, id + "F8", {"entities" : qUnion([Q0]), "transformType" : TransformType.TRANSLATION_3D, "dx" : -160 * mm, "dy" : 0 * mm, "dz" : 0 * mm, "makeCopy" : true});
        }
        {
            var Q0;
            Q0=makeQuery(id+"F7.opExtrude","SWEPT_FACE",FACE,{"disambiguationData":[OSD([sQuery(id+"F6.wireOp",EDGE,"E125")])]});
            var sketch = newSketch(context, id + "F9", { "sketchPlane" : qUnion([Q0])});
            skLineSegment(sketch, "E140.0", {"start": v(-122.7, 49.25) * mm, "end": v(-117.7, 49.25) * mm});
            skLineSegment(sketch, "E140.1", {"start": v(-122.7, 49.25) * mm, "end": v(-122.7, -48.05) * mm});
            skLineSegment(sketch, "E140.2", {"start": v(-122.7, -48.05) * mm, "end": v(-117.7, -48.05) * mm});
            skLineSegment(sketch, "E141", {"start": v(-132.7, 39.25) * mm, "end": v(-132.7, 29.25) * mm});
            skLineSegment(sketch, "E142", {"start": v(-122.7, 0.6) * mm, "end": v(-117.7, 0.6) * mm, "construction": true});
            skLineSegment(sketch, "E143.MirrorCS", {"start": v(-132.7, -38.05) * mm, "end": v(-132.7, -28.05) * mm});
            skPoint(sketch, "E144", {"position": v(-127.7, 34.25) * mm});
            skPoint(sketch, "E145", {"position": v(-127.7, -33.05) * mm});
            skLineSegment(sketch, "E146", {"start": v(-132.7, 39.25) * mm, "end": v(-122.7, 49.25) * mm});
            skPoint(sketch, "E147", {"position": v(-122.7, 19.25) * mm});
            skLineSegment(sketch, "E148", {"start": v(-132.7, 29.25) * mm, "end": v(-122.7, 19.25) * mm});
            skPoint(sketch, "E149.orphan", {"position": v(-122.7, 39.25) * mm});
            skPoint(sketch, "E150.end.orphan", {"position": v(-122.7, 29.25) * mm});
            skLineSegment(sketch, "E151.MirrorCS", {"start": v(-132.7, -38.05) * mm, "end": v(-122.7, -48.05) * mm});
            skLineSegment(sketch, "E152.MirrorCS", {"start": v(-132.7, -28.05) * mm, "end": v(-122.7, -18.05) * mm});
            skPoint(sketch, "E153.orphan", {"position": v(-122.7, -28.05) * mm});
            skPoint(sketch, "E154.MirrorCS.start.orphan", {"position": v(-122.7, -38.05) * mm});
            skPoint(sketch, "E155", {"position": v(-122.7, 49.25) * mm});
            skPoint(sketch, "E156", {"position": v(-122.7, -48.05) * mm});
            skSolve(sketch);
        }
        {
            var Q0;
            Q0=makeQuery(id+"F8.opPattern","COPY",FACE,{"derivedFrom":makeQuery(id+"F7.opExtrude","SWEPT_FACE",FACE,{"disambiguationData":[OSD([sQuery(id+"F6.wireOp",EDGE,"E125")])]}),"instanceName":"1"});
            var sketch = newSketch(context, id + "F10", { "sketchPlane" : qUnion([Q0])});
            skLineSegment(sketch, "E157.0", {"start": v(42.3, -48.05) * mm, "end": v(37.3, -48.05) * mm});
            skLineSegment(sketch, "E157.1", {"start": v(42.3, -48.05) * mm, "end": v(42.3, 49.25) * mm});
            skLineSegment(sketch, "E157.2", {"start": v(42.3, 49.25) * mm, "end": v(37.3, 49.25) * mm});
            skLineSegment(sketch, "E158", {"start": v(52.3, -38.05) * mm, "end": v(52.3, -28.05) * mm});
            skLineSegment(sketch, "E159", {"start": v(42.3, 0.6) * mm, "end": v(37.3, 0.6) * mm, "construction": true});
            skLineSegment(sketch, "E160.MirrorCS", {"start": v(52.3, 39.25) * mm, "end": v(52.3, 29.25) * mm});
            skPoint(sketch, "E161", {"position": v(47.3, -33.05) * mm});
            skPoint(sketch, "E162", {"position": v(47.3, 34.25) * mm});
            skLineSegment(sketch, "E163", {"start": v(52.3, -38.05) * mm, "end": v(42.3, -48.05) * mm});
            skPoint(sketch, "E164", {"position": v(42.3, -18.05) * mm});
            skLineSegment(sketch, "E165", {"start": v(52.3, -28.05) * mm, "end": v(42.3, -18.05) * mm});
            skPoint(sketch, "E166.orphan", {"position": v(42.3, -38.05) * mm});
            skPoint(sketch, "E167.end.orphan", {"position": v(42.3, -28.05) * mm});
            skLineSegment(sketch, "E168.MirrorCS", {"start": v(52.3, 39.25) * mm, "end": v(42.3, 49.25) * mm});
            skLineSegment(sketch, "E169.MirrorCS", {"start": v(52.3, 29.25) * mm, "end": v(42.3, 19.25) * mm});
            skPoint(sketch, "E170.orphan", {"position": v(42.3, 29.25) * mm});
            skPoint(sketch, "E171.MirrorCS.start.orphan", {"position": v(42.3, 39.25) * mm});
            skPoint(sketch, "E172", {"position": v(42.3, -48.05) * mm});
            skPoint(sketch, "E173", {"position": v(42.3, 49.25) * mm});
            skSolve(sketch);
        }
        {
            var Q0;
            Q0=makeQuery(id+"F9.imprint","IMPRINT",FACE,{"disambiguationData":[TD([[makeQuery(id+"F9.imprint","IMPRINT",EDGE,{"derivedFrom":sQuery(id+"F9.wireOp",EDGE,"E141")}),1.0]])]});
            var Q1;
            Q1=makeQuery(id+"F9.imprint","IMPRINT",FACE,{"disambiguationData":[TD([[makeQuery(id+"F9.imprint","IMPRINT",EDGE,{"derivedFrom":sQuery(id+"F9.wireOp",EDGE,"E143.MirrorCS")}),-1.0]])]});
            extrude(context, id + "F11", {"entities" : qUnion([Q0, Q1]), "operationType" : NewBodyOperationType.ADD, "oppositeDirection" : true, "depth" : 5 * mm, "offsetDistance" : 25 * mm});
        }
        {
            var Q0;
            Q0=makeQuery(id+"F10.imprint","IMPRINT",FACE,{"disambiguationData":[TD([[makeQuery(id+"F10.imprint","IMPRINT",EDGE,{"derivedFrom":sQuery(id+"F10.wireOp",EDGE,"E160.MirrorCS")}),-1.0]])]});
            var Q1;
            Q1=makeQuery(id+"F10.imprint","IMPRINT",FACE,{"disambiguationData":[TD([[makeQuery(id+"F10.imprint","IMPRINT",EDGE,{"derivedFrom":sQuery(id+"F10.wireOp",EDGE,"E158")}),1.0]])]});
            extrude(context, id + "F12", {"entities" : qUnion([Q0, Q1]), "operationType" : NewBodyOperationType.ADD, "oppositeDirection" : true, "depth" : 5 * mm, "offsetDistance" : 25 * mm});
        }
        {
            var Q0;
            Q0=makeQuery(id+"F12.opExtrude","CAP_FACE",FACE,{"disambiguationData":[OSD([sQuery(id+"F10.wireOp",EDGE,"E157.1"),sQuery(id+"F10.wireOp",EDGE,"E160.MirrorCS"),sQuery(id+"F10.wireOp",EDGE,"E168.MirrorCS"),sQuery(id+"F10.wireOp",EDGE,"E169.MirrorCS")])],"isStart":false});
            var sketch = newSketch(context, id + "F13", { "sketchPlane" : qUnion([Q0])});
            skPoint(sketch, "E174.0", {"position": v(-47.3, 34.25) * mm});
            skPoint(sketch, "E174.1", {"position": v(-47.3, -33.05) * mm});
            skSolve(sketch);
        }
        {
            var Q0;
            Q0=sQuery(id+"F13.wireOp",VERTEX,"E174.0");
            var Q1;
            Q1=sQuery(id+"F13.wireOp",VERTEX,"E174.1");
            var Q2;
            Q2=makeQuery(id+"F8.opPattern","COPY",BODY,{"derivedFrom":makeQuery(id+"F7.opExtrude","SWEPT_BODY",BODY,{"disambiguationData":[OSD([sQuery(id+"F6.wireOp",EDGE,"E105.0"),sQuery(id+"F6.wireOp",EDGE,"E105.1"),sQuery(id+"F6.wireOp",EDGE,"E105.2"),sQuery(id+"F6.wireOp",EDGE,"E106.0"),sQuery(id+"F6.wireOp",EDGE,"E106.1"),sQuery(id+"F6.wireOp",EDGE,"E106.2"),sQuery(id+"F6.wireOp",EDGE,"E107.0"),sQuery(id+"F6.wireOp",EDGE,"E107.1"),sQuery(id+"F6.wireOp",EDGE,"E107.2"),sQuery(id+"F6.wireOp",EDGE,"E108.0"),sQuery(id+"F6.wireOp",EDGE,"E109"),sQuery(id+"F6.wireOp",EDGE,"E110"),sQuery(id+"F6.wireOp",EDGE,"E111.trimOffspring"),sQuery(id+"F6.wireOp",EDGE,"E112"),sQuery(id+"F6.wireOp",EDGE,"E113"),sQuery(id+"F6.wireOp",EDGE,"E114"),sQuery(id+"F6.wireOp",EDGE,"E115"),sQuery(id+"F6.wireOp",EDGE,"E116.trimOffspring"),sQuery(id+"F6.wireOp",EDGE,"E117"),sQuery(id+"F6.wireOp",EDGE,"E118"),sQuery(id+"F6.wireOp",EDGE,"E119"),sQuery(id+"F6.wireOp",EDGE,"E120"),sQuery(id+"F6.wireOp",EDGE,"E121.trimOffspring"),sQuery(id+"F6.wireOp",EDGE,"E122"),sQuery(id+"F6.wireOp",EDGE,"E123"),sQuery(id+"F6.wireOp",EDGE,"E124"),sQuery(id+"F6.wireOp",EDGE,"E125"),sQuery(id+"F6.wireOp",EDGE,"E126"),sQuery(id+"F6.wireOp",EDGE,"E127"),sQuery(id+"F6.wireOp",EDGE,"E128"),sQuery(id+"F6.wireOp",EDGE,"E129"),sQuery(id+"F6.wireOp",EDGE,"E130"),sQuery(id+"F6.wireOp",EDGE,"E131.0"),sQuery(id+"F6.wireOp",EDGE,"E132.trimOffspring"),sQuery(id+"F6.wireOp",EDGE,"E133"),sQuery(id+"F6.wireOp",EDGE,"E134"),sQuery(id+"F6.wireOp",EDGE,"E135.trimOffspring"),sQuery(id+"F6.wireOp",EDGE,"E136.trimOffspring"),sQuery(id+"F6.wireOp",EDGE,"E137.trimOffspring"),sQuery(id+"F6.wireOp",EDGE,"E138.trimOffspring"),sQuery(id+"F6.wireOp",EDGE,"E139.trimOffspring")])]}),"instanceName":"1"});
            hole(context, id + "F14", {"style" : HoleStyle.C_SINK, "endStyle" : HoleEndStyle.THROUGH, "holeDiameter" : 3.5 * mm, "cSinkDiameter" : 7 * mm, "cSinkAngle" : 82 * degree, "majorDiameter" : 5 * mm, "isTappedThrough" : true, "tappedDepth" : 12 * mm, "tapClearance" : 3, "locations" : qUnion([Q0, Q1]), "scope" : qUnion([Q2]), "startStyle" : HoleStartStyle.SKETCH});
        }
        {
            var Q0;
            Q0=makeQuery(id+"F11.opExtrude","CAP_FACE",FACE,{"disambiguationData":[OSD([sQuery(id+"F9.wireOp",EDGE,"E140.1"),sQuery(id+"F9.wireOp",EDGE,"E141"),sQuery(id+"F9.wireOp",EDGE,"E146"),sQuery(id+"F9.wireOp",EDGE,"E148")])],"isStart":false});
            var sketch = newSketch(context, id + "F15", { "sketchPlane" : qUnion([Q0])});
            skPoint(sketch, "E175.0", {"position": v(127.7, 34.25) * mm});
            skPoint(sketch, "E175.1", {"position": v(127.7, -33.05) * mm});
            skSolve(sketch);
        }
        {
            var Q0;
            Q0=sQuery(id+"F15.wireOp",VERTEX,"E175.0");
            var Q1;
            Q1=sQuery(id+"F15.wireOp",VERTEX,"E175.1");
            var Q2;
            Q2=makeQuery(id+"F7.opExtrude","SWEPT_BODY",BODY,{"disambiguationData":[OSD([sQuery(id+"F6.wireOp",EDGE,"E105.0"),sQuery(id+"F6.wireOp",EDGE,"E105.1"),sQuery(id+"F6.wireOp",EDGE,"E105.2"),sQuery(id+"F6.wireOp",EDGE,"E106.0"),sQuery(id+"F6.wireOp",EDGE,"E106.1"),sQuery(id+"F6.wireOp",EDGE,"E106.2"),sQuery(id+"F6.wireOp",EDGE,"E107.0"),sQuery(id+"F6.wireOp",EDGE,"E107.1"),sQuery(id+"F6.wireOp",EDGE,"E107.2"),sQuery(id+"F6.wireOp",EDGE,"E108.0"),sQuery(id+"F6.wireOp",EDGE,"E109"),sQuery(id+"F6.wireOp",EDGE,"E110"),sQuery(id+"F6.wireOp",EDGE,"E111.trimOffspring"),sQuery(id+"F6.wireOp",EDGE,"E112"),sQuery(id+"F6.wireOp",EDGE,"E113"),sQuery(id+"F6.wireOp",EDGE,"E114"),sQuery(id+"F6.wireOp",EDGE,"E115"),sQuery(id+"F6.wireOp",EDGE,"E116.trimOffspring"),sQuery(id+"F6.wireOp",EDGE,"E117"),sQuery(id+"F6.wireOp",EDGE,"E118"),sQuery(id+"F6.wireOp",EDGE,"E119"),sQuery(id+"F6.wireOp",EDGE,"E120"),sQuery(id+"F6.wireOp",EDGE,"E121.trimOffspring"),sQuery(id+"F6.wireOp",EDGE,"E122"),sQuery(id+"F6.wireOp",EDGE,"E123"),sQuery(id+"F6.wireOp",EDGE,"E124"),sQuery(id+"F6.wireOp",EDGE,"E125"),sQuery(id+"F6.wireOp",EDGE,"E126"),sQuery(id+"F6.wireOp",EDGE,"E127"),sQuery(id+"F6.wireOp",EDGE,"E128"),sQuery(id+"F6.wireOp",EDGE,"E129"),sQuery(id+"F6.wireOp",EDGE,"E130"),sQuery(id+"F6.wireOp",EDGE,"E131.0"),sQuery(id+"F6.wireOp",EDGE,"E132.trimOffspring"),sQuery(id+"F6.wireOp",EDGE,"E133"),sQuery(id+"F6.wireOp",EDGE,"E134"),sQuery(id+"F6.wireOp",EDGE,"E135.trimOffspring"),sQuery(id+"F6.wireOp",EDGE,"E136.trimOffspring"),sQuery(id+"F6.wireOp",EDGE,"E137.trimOffspring"),sQuery(id+"F6.wireOp",EDGE,"E138.trimOffspring"),sQuery(id+"F6.wireOp",EDGE,"E139.trimOffspring")])]});
            hole(context, id + "F16", {"style" : HoleStyle.C_SINK, "endStyle" : HoleEndStyle.THROUGH, "holeDiameter" : 3.5 * mm, "cSinkDiameter" : 7 * mm, "cSinkAngle" : 82 * degree, "majorDiameter" : 5 * mm, "isTappedThrough" : true, "tappedDepth" : 12 * mm, "tapClearance" : 3, "locations" : qUnion([Q0, Q1]), "scope" : qUnion([Q2]), "startStyle" : HoleStartStyle.SKETCH});
        }
        {
            var Q0;
            Q0=makeQuery(id+"F1.opExtrude","CAP_FACE",FACE,{"disambiguationData":[OSD([sQuery(id+"F0.wireOp",EDGE,"E0"),sQuery(id+"F0.wireOp",EDGE,"E1.0.1.0"),sQuery(id+"F0.wireOp",EDGE,"E1.1.0.0"),sQuery(id+"F0.wireOp",EDGE,"E1.1.1.0"),sQuery(id+"F0.wireOp",EDGE,"E2"),sQuery(id+"F0.wireOp",EDGE,"E3.0.1.0"),sQuery(id+"F0.wireOp",EDGE,"E3.1.0.0"),sQuery(id+"F0.wireOp",EDGE,"E3.1.1.0"),sQuery(id+"F0.wireOp",EDGE,"E4"),sQuery(id+"F0.wireOp",EDGE,"E5.0.1.0"),sQuery(id+"F0.wireOp",EDGE,"E5.0.2.0"),sQuery(id+"F0.wireOp",EDGE,"E5.1.0.0"),sQuery(id+"F0.wireOp",EDGE,"E5.1.1.0"),sQuery(id+"F0.wireOp",EDGE,"E5.1.2.0"),sQuery(id+"F0.wireOp",EDGE,"E5.2.0.0"),sQuery(id+"F0.wireOp",EDGE,"E5.2.1.0"),sQuery(id+"F0.wireOp",EDGE,"E5.2.2.0"),sQuery(id+"F0.wireOp",EDGE,"E6"),sQuery(id+"F0.wireOp",EDGE,"E7.1.0.0"),sQuery(id+"F0.wireOp",EDGE,"E7.2.0.0"),sQuery(id+"F0.wireOp",EDGE,"E7.3.0.0"),sQuery(id+"F0.wireOp",EDGE,"E7.4.0.0"),sQuery(id+"F0.wireOp",EDGE,"E7.5.0.0"),sQuery(id+"F0.wireOp",EDGE,"E8.0.6.0"),sQuery(id+"F0.wireOp",EDGE,"E8.0.7.0"),sQuery(id+"F0.wireOp",EDGE,"E8.0.8.0"),sQuery(id+"F0.wireOp",EDGE,"E8.0.9.0"),sQuery(id+"F0.wireOp",EDGE,"E9.0.10.0"),sQuery(id+"F0.wireOp",EDGE,"E10.1.0.0"),sQuery(id+"F0.wireOp",EDGE,"E10.2.0.0"),sQuery(id+"F0.wireOp",EDGE,"E13"),sQuery(id+"F0.wireOp",EDGE,"E14"),sQuery(id+"F0.wireOp",EDGE,"E15"),sQuery(id+"F0.wireOp",EDGE,"E17"),sQuery(id+"F0.wireOp",EDGE,"E18"),sQuery(id+"F0.wireOp",EDGE,"E19"),sQuery(id+"F0.wireOp",EDGE,"E20"),sQuery(id+"F0.wireOp",EDGE,"E21"),sQuery(id+"F0.wireOp",EDGE,"E22"),sQuery(id+"F0.wireOp",EDGE,"E23.1.0.0"),sQuery(id+"F0.wireOp",EDGE,"E23.2.0.0"),sQuery(id+"F0.wireOp",EDGE,"E23.3.0.0")])],"isStart":false});
            var sketch = newSketch(context, id + "F17", { "sketchPlane" : qUnion([Q0])});
            skLineSegment(sketch, "E176.1", {"start": v(126.2, 95.35) * mm, "end": v(126.2, 15.35) * mm});
            skLineSegment(sketch, "E176.2", {"start": v(-45.8, 15.35) * mm, "end": v(-45.8, 95.35) * mm});
            skArc(sketch, "E177.0", {"start": v(-33.64, 29.85) * mm, "mid": v(-19.8, 20.45) * mm, "end": v(-5.95, 29.85) * mm});
            skArc(sketch, "E178.0", {"start": v(0.42, 29.85) * mm, "mid": v(7.7, 25.64) * mm, "end": v(14.98, 29.85) * mm});
            skArc(sketch, "E179.0", {"start": v(20.67, 29.85) * mm, "mid": v(32.7, 20.45) * mm, "end": v(44.74, 29.85) * mm});
            skArc(sketch, "E180.0", {"start": v(50.12, 29.85) * mm, "mid": v(55.2, 26.95) * mm, "end": v(60.28, 29.85) * mm});
            skArc(sketch, "E181.0", {"start": v(65.67, 29.85) * mm, "mid": v(77.7, 20.45) * mm, "end": v(89.74, 29.85) * mm});
            skArc(sketch, "E182.0", {"start": v(94.86, 29.85) * mm, "mid": v(102.7, 24.45) * mm, "end": v(110.55, 29.85) * mm});
            skLineSegment(sketch, "E183.0", {"start": v(126.2, 14.85) * mm, "end": v(-45.8, 14.85) * mm});
            skLineSegment(sketch, "E184", {"start": v(-45.8, 29.85) * mm, "end": v(126.2, 29.85) * mm});
            skLineSegment(sketch, "E185", {"start": v(-37.3, -25.15) * mm, "end": v(117.7, -25.15) * mm});
            skLineSegment(sketch, "E186.0", {"start": v(-37.3, 29.85) * mm, "end": v(-37.3, 29.75) * mm});
            skLineSegment(sketch, "E186.1", {"start": v(117.7, 29.85) * mm, "end": v(117.7, 29.75) * mm});
            skLineSegment(sketch, "E187", {"start": v(-37.3, 29.75) * mm, "end": v(-37.3, -25.15) * mm});
            skLineSegment(sketch, "E188", {"start": v(117.7, 29.75) * mm, "end": v(117.7, -25.15) * mm});
            skPoint(sketch, "E189.orphan", {"position": v(-37.3, 50.95) * mm});
            skPoint(sketch, "E190.orphan", {"position": v(117.7, 50.95) * mm});
            skPoint(sketch, "E191.orphan", {"position": v(126.2, -25.15) * mm});
            skSolve(sketch);
        }
        {
            var Q0;
            {var subQ0=sQuery(id+"F17.wireOp",EDGE,"E177.0");Q0=makeQuery(id+"F17.imprint","IMPRINT",FACE,{"disambiguationData":[TD([[makeQuery(id+"F17.imprint","IMPRINT",EDGE,{"derivedFrom":subQ0}),1.0]])]});}
            var Q1;
            {var subQ0=sQuery(id+"F17.wireOp",EDGE,"E178.0");Q1=makeQuery(id+"F17.imprint","IMPRINT",FACE,{"disambiguationData":[TD([[makeQuery(id+"F17.imprint","IMPRINT",EDGE,{"derivedFrom":subQ0}),1.0]])]});}
            var Q2;
            {var subQ0=sQuery(id+"F17.wireOp",EDGE,"E179.0");Q2=makeQuery(id+"F17.imprint","IMPRINT",FACE,{"disambiguationData":[TD([[makeQuery(id+"F17.imprint","IMPRINT",EDGE,{"derivedFrom":subQ0}),1.0]])]});}
            var Q3;
            {var subQ0=sQuery(id+"F17.wireOp",EDGE,"E180.0");Q3=makeQuery(id+"F17.imprint","IMPRINT",FACE,{"disambiguationData":[TD([[makeQuery(id+"F17.imprint","IMPRINT",EDGE,{"derivedFrom":subQ0}),1.0]])]});}
            var Q4;
            {var subQ0=sQuery(id+"F17.wireOp",EDGE,"E181.0");Q4=makeQuery(id+"F17.imprint","IMPRINT",FACE,{"disambiguationData":[TD([[makeQuery(id+"F17.imprint","IMPRINT",EDGE,{"derivedFrom":subQ0}),1.0]])]});}
            var Q5;
            {var subQ0=sQuery(id+"F17.wireOp",EDGE,"E182.0");Q5=makeQuery(id+"F17.imprint","IMPRINT",FACE,{"disambiguationData":[TD([[makeQuery(id+"F17.imprint","IMPRINT",EDGE,{"derivedFrom":subQ0}),1.0]])]});}
            extrude(context, id + "F18", {"entities" : qUnion([Q0, Q1, Q2, Q3, Q4, Q5]), "oppositeDirection" : true, "depth" : 12 * mm, "offsetDistance" : 25 * mm});
        }
        {
            var Q0;
            Q0=makeQuery(id+"F1.opExtrude","CAP_FACE",FACE,{"disambiguationData":[OSD([sQuery(id+"F0.wireOp",EDGE,"E0"),sQuery(id+"F0.wireOp",EDGE,"E1.0.1.0"),sQuery(id+"F0.wireOp",EDGE,"E1.1.0.0"),sQuery(id+"F0.wireOp",EDGE,"E1.1.1.0"),sQuery(id+"F0.wireOp",EDGE,"E2"),sQuery(id+"F0.wireOp",EDGE,"E3.0.1.0"),sQuery(id+"F0.wireOp",EDGE,"E3.1.0.0"),sQuery(id+"F0.wireOp",EDGE,"E3.1.1.0"),sQuery(id+"F0.wireOp",EDGE,"E4"),sQuery(id+"F0.wireOp",EDGE,"E5.0.1.0"),sQuery(id+"F0.wireOp",EDGE,"E5.0.2.0"),sQuery(id+"F0.wireOp",EDGE,"E5.1.0.0"),sQuery(id+"F0.wireOp",EDGE,"E5.1.1.0"),sQuery(id+"F0.wireOp",EDGE,"E5.1.2.0"),sQuery(id+"F0.wireOp",EDGE,"E5.2.0.0"),sQuery(id+"F0.wireOp",EDGE,"E5.2.1.0"),sQuery(id+"F0.wireOp",EDGE,"E5.2.2.0"),sQuery(id+"F0.wireOp",EDGE,"E6"),sQuery(id+"F0.wireOp",EDGE,"E7.1.0.0"),sQuery(id+"F0.wireOp",EDGE,"E7.2.0.0"),sQuery(id+"F0.wireOp",EDGE,"E7.3.0.0"),sQuery(id+"F0.wireOp",EDGE,"E7.4.0.0"),sQuery(id+"F0.wireOp",EDGE,"E7.5.0.0"),sQuery(id+"F0.wireOp",EDGE,"E8.0.6.0"),sQuery(id+"F0.wireOp",EDGE,"E8.0.7.0"),sQuery(id+"F0.wireOp",EDGE,"E8.0.8.0"),sQuery(id+"F0.wireOp",EDGE,"E8.0.9.0"),sQuery(id+"F0.wireOp",EDGE,"E9.0.10.0"),sQuery(id+"F0.wireOp",EDGE,"E10.1.0.0"),sQuery(id+"F0.wireOp",EDGE,"E10.2.0.0"),sQuery(id+"F0.wireOp",EDGE,"E13"),sQuery(id+"F0.wireOp",EDGE,"E14"),sQuery(id+"F0.wireOp",EDGE,"E15"),sQuery(id+"F0.wireOp",EDGE,"E17"),sQuery(id+"F0.wireOp",EDGE,"E18"),sQuery(id+"F0.wireOp",EDGE,"E19"),sQuery(id+"F0.wireOp",EDGE,"E20"),sQuery(id+"F0.wireOp",EDGE,"E21"),sQuery(id+"F0.wireOp",EDGE,"E22"),sQuery(id+"F0.wireOp",EDGE,"E23.1.0.0"),sQuery(id+"F0.wireOp",EDGE,"E23.2.0.0"),sQuery(id+"F0.wireOp",EDGE,"E23.3.0.0")])],"isStart":true});
            var sketch = newSketch(context, id + "F19", { "sketchPlane" : qUnion([Q0])});
            skLineSegment(sketch, "E192.0", {"start": v(33.64, 29.85) * mm, "end": v(5.95, 29.85) * mm});
            skLineSegment(sketch, "E192.1", {"start": v(-126.2, 15.35) * mm, "end": v(45.8, 15.35) * mm});
            skLineSegment(sketch, "E192.2", {"start": v(37.3, 89.75) * mm, "end": v(37.3, 20.95) * mm});
            skLineSegment(sketch, "E192.3", {"start": v(-117.7, 89.75) * mm, "end": v(-117.7, 20.95) * mm});
            skLineSegment(sketch, "E193", {"start": v(5.95, 29.85) * mm, "end": v(-117.7, 29.85) * mm});
            skLineSegment(sketch, "E194", {"start": v(33.64, 29.85) * mm, "end": v(37.3, 29.85) * mm});
            skLineSegment(sketch, "E195", {"start": v(-117.7, 20.95) * mm, "end": v(-117.7, 15.35) * mm});
            skLineSegment(sketch, "E196", {"start": v(37.3, 20.95) * mm, "end": v(37.3, 15.35) * mm});
            skSolve(sketch);
        }
        {
            var Q0;
            Q0 = qSketchRegion(id + "F19", true);
            extrude(context, id + "F20", {"entities" : qUnion([Q0]), "operationType" : NewBodyOperationType.ADD, "depth" : 4 * mm, "offsetDistance" : 25 * mm});
        }
        {
            var Q0;
            Q0=makeQuery(id+"F20.opExtrude","SWEPT_FACE",FACE,{"disambiguationData":[OSD([sQuery(id+"F19.wireOp",EDGE,"E192.1")])]});
            extrude(context, id + "F21", {"entities" : qUnion([Q0]), "operationType" : NewBodyOperationType.ADD, "depth" : 1 * mm, "offsetDistance" : 25 * mm});
        }
        {
            var Q0;
            {var subQ5=sQuery(id+"F17.wireOp",EDGE,"E185");Q0=makeQuery(id+"F17.imprint","IMPRINT",FACE,{"disambiguationData":[TD([[makeQuery(id+"F17.imprint","IMPRINT",EDGE,{"derivedFrom":subQ5}),1.0]])]});}
            extrude(context, id + "F22", {"entities" : qUnion([Q0]), "operationType" : NewBodyOperationType.ADD, "oppositeDirection" : true, "depth" : 12 * mm, "offsetDistance" : 25 * mm});
        }
        {
            var Q0;
            Q0=makeQuery(id+"F17.imprint","IMPRINT",FACE,{"disambiguationData":[TD([[makeQuery(id+"F17.imprint","IMPRINT",EDGE,{"derivedFrom":makeQuery(id+"F1.opExtrude","CAP_EDGE",EDGE,{"disambiguationData":[OSD([sQuery(id+"F0.wireOp",EDGE,"E0")])],"isStart":false})}),1.0]])]});
            var Q1;
            Q1=makeQuery(id+"F17.imprint","IMPRINT",FACE,{"disambiguationData":[TD([[makeQuery(id+"F17.imprint","IMPRINT",EDGE,{"derivedFrom":makeQuery(id+"F1.opExtrude","CAP_EDGE",EDGE,{"disambiguationData":[OSD([sQuery(id+"F0.wireOp",EDGE,"E1.1.0.0")])],"isStart":false})}),1.0]])]});
            var Q2;
            Q2=makeQuery(id+"F17.imprint","IMPRINT",FACE,{"disambiguationData":[TD([[makeQuery(id+"F17.imprint","IMPRINT",EDGE,{"derivedFrom":makeQuery(id+"F1.opExtrude","CAP_EDGE",EDGE,{"disambiguationData":[OSD([sQuery(id+"F0.wireOp",EDGE,"E2")])],"isStart":false})}),1.0]])]});
            var Q3;
            Q3=makeQuery(id+"F17.imprint","IMPRINT",FACE,{"disambiguationData":[TD([[makeQuery(id+"F17.imprint","IMPRINT",EDGE,{"derivedFrom":makeQuery(id+"F1.opExtrude","CAP_EDGE",EDGE,{"disambiguationData":[OSD([sQuery(id+"F0.wireOp",EDGE,"E3.1.0.0")])],"isStart":false})}),1.0]])]});
            var Q4;
            Q4=makeQuery(id+"F17.imprint","IMPRINT",FACE,{"disambiguationData":[TD([[makeQuery(id+"F17.imprint","IMPRINT",EDGE,{"derivedFrom":makeQuery(id+"F1.opExtrude","CAP_EDGE",EDGE,{"disambiguationData":[OSD([sQuery(id+"F0.wireOp",EDGE,"E4")])],"isStart":false})}),1.0]])]});
            var Q5;
            Q5=makeQuery(id+"F17.imprint","IMPRINT",FACE,{"disambiguationData":[TD([[makeQuery(id+"F17.imprint","IMPRINT",EDGE,{"derivedFrom":makeQuery(id+"F1.opExtrude","CAP_EDGE",EDGE,{"disambiguationData":[OSD([sQuery(id+"F0.wireOp",EDGE,"E5.1.0.0")])],"isStart":false})}),1.0]])]});
            var Q6;
            Q6=makeQuery(id+"F17.imprint","IMPRINT",FACE,{"disambiguationData":[TD([[makeQuery(id+"F17.imprint","IMPRINT",EDGE,{"derivedFrom":makeQuery(id+"F1.opExtrude","CAP_EDGE",EDGE,{"disambiguationData":[OSD([sQuery(id+"F0.wireOp",EDGE,"E5.2.0.0")])],"isStart":false})}),1.0]])]});
            extrude(context, id + "F23", {"entities" : qUnion([Q0, Q1, Q2, Q3, Q4, Q5, Q6]), "operationType" : NewBodyOperationType.REMOVE, "oppositeDirection" : true, "depth" : 25 * mm, "offsetDistance" : 25 * mm});
        }
        {
            var Q0;
            Q0=makeQuery(id+"F22.opExtrude","SWEPT_FACE",FACE,{"disambiguationData":[OSD([sQuery(id+"F17.wireOp",EDGE,"E185")])]});
            extrude(context, id + "F24", {"entities" : qUnion([Q0]), "operationType" : NewBodyOperationType.REMOVE, "oppositeDirection" : true, "depth" : 25 * mm, "offsetDistance" : 25 * mm});
        }
        {
            var Q0;
            Q0=makeQuery(id+"F24.boolean.opBoolean","COPY",FACE,{"derivedFrom":makeQuery(id+"F24.opExtrude","CAP_FACE",FACE,{"disambiguationData":[OSD([sQuery(id+"F17.wireOp",EDGE,"E185")])],"isStart":false})});
            var sketch = newSketch(context, id + "F25", { "sketchPlane" : qUnion([Q0])});
            skLineSegment(sketch, "E197.0", {"start": v(-37.3, 8) * mm, "end": v(117.7, 8) * mm});
            skLineSegment(sketch, "E198.0", {"start": v(-36.6, 8) * mm, "end": v(-33, 8) * mm});
            skLineSegment(sketch, "E199.0", {"start": v(-6.6, 8) * mm, "end": v(-3, 8) * mm, "construction": true});
            skLineSegment(sketch, "E199.1", {"start": v(18.4, 8) * mm, "end": v(22, 8) * mm, "construction": true});
            skLineSegment(sketch, "E199.2", {"start": v(43.4, 8) * mm, "end": v(47, 8) * mm, "construction": true});
            skLineSegment(sketch, "E199.3", {"start": v(63.4, 8) * mm, "end": v(67, 8) * mm, "construction": true});
            skLineSegment(sketch, "E199.4", {"start": v(88.4, 8) * mm, "end": v(92, 8) * mm, "construction": true});
            skLineSegment(sketch, "E199.5", {"start": v(113.4, 8) * mm, "end": v(117, 8) * mm, "construction": true});
            skLineSegment(sketch, "E200", {"start": v(-33, 8) * mm, "end": v(-6.6, 8) * mm, "construction": true});
            skLineSegment(sketch, "E201", {"start": v(-3, 8) * mm, "end": v(18.4, 8) * mm, "construction": true});
            skLineSegment(sketch, "E202", {"start": v(22, 8) * mm, "end": v(43.4, 8) * mm, "construction": true});
            skLineSegment(sketch, "E203", {"start": v(47, 8) * mm, "end": v(63.4, 8) * mm, "construction": true});
            skLineSegment(sketch, "E204", {"start": v(67, 8) * mm, "end": v(88.4, 8) * mm, "construction": true});
            skLineSegment(sketch, "E205", {"start": v(92, 8) * mm, "end": v(113.4, 8) * mm, "construction": true});
            skPoint(sketch, "E206", {"position": v(-19.8, 8) * mm});
            skPoint(sketch, "E207", {"position": v(7.7, 8) * mm});
            skPoint(sketch, "E208", {"position": v(32.7, 8) * mm});
            skPoint(sketch, "E209", {"position": v(55.2, 8) * mm});
            skPoint(sketch, "E210", {"position": v(77.7, 8) * mm});
            skPoint(sketch, "E211", {"position": v(102.7, 8) * mm});
            skArc(sketch, "E212", {"start": v(-14.8, 8) * mm, "mid": v(-19.8, 13) * mm, "end": v(-24.8, 8) * mm});
            skArc(sketch, "E213", {"start": v(-16.8, 8) * mm, "mid": v(-19.8, 11) * mm, "end": v(-22.8, 8) * mm});
            skArc(sketch, "E214", {"start": v(12.7, 8) * mm, "mid": v(7.7, 13) * mm, "end": v(2.7, 8) * mm});
            skArc(sketch, "E215", {"start": v(10.7, 8) * mm, "mid": v(7.7, 11) * mm, "end": v(4.7, 8) * mm});
            skArc(sketch, "E216", {"start": v(37.7, 8) * mm, "mid": v(32.7, 13) * mm, "end": v(27.7, 8) * mm});
            skArc(sketch, "E217", {"start": v(35.7, 8) * mm, "mid": v(32.7, 11) * mm, "end": v(29.7, 8) * mm});
            skArc(sketch, "E218", {"start": v(60.2, 8) * mm, "mid": v(55.2, 13) * mm, "end": v(50.2, 8) * mm});
            skArc(sketch, "E219", {"start": v(58.2, 8) * mm, "mid": v(55.2, 11) * mm, "end": v(52.2, 8) * mm});
            skArc(sketch, "E220", {"start": v(82.7, 8) * mm, "mid": v(77.7, 13) * mm, "end": v(72.7, 8) * mm});
            skArc(sketch, "E221", {"start": v(80.7, 8) * mm, "mid": v(77.7, 11) * mm, "end": v(74.7, 8) * mm});
            skArc(sketch, "E222", {"start": v(107.7, 8) * mm, "mid": v(102.7, 13) * mm, "end": v(97.7, 8) * mm});
            skArc(sketch, "E223", {"start": v(105.7, 8) * mm, "mid": v(102.7, 11) * mm, "end": v(99.7, 8) * mm});
            skLineSegment(sketch, "E224.0", {"start": v(117.7, -4) * mm, "end": v(117.7, 8) * mm});
            skLineSegment(sketch, "E224.1", {"start": v(-37.3, -4) * mm, "end": v(117.7, -4) * mm});
            skLineSegment(sketch, "E224.2", {"start": v(-37.3, -4) * mm, "end": v(-37.3, 8) * mm});
            skLineSegment(sketch, "E225.bottom", {"start": v(-33.48, 4.5) * mm, "end": v(114.46, 4.5) * mm});
            skLineSegment(sketch, "E225.top", {"start": v(-33.48, -0.5) * mm, "end": v(114.46, -0.5) * mm});
            skLineSegment(sketch, "E225.left", {"start": v(-33.48, 4.5) * mm, "end": v(-33.48, -0.5) * mm});
            skLineSegment(sketch, "E225.right", {"start": v(114.46, 4.5) * mm, "end": v(114.46, -0.5) * mm});
            skLineSegment(sketch, "E226", {"start": v(-19.8, 4.5) * mm, "end": v(-19.8, -0.5) * mm});
            skLineSegment(sketch, "E227", {"start": v(7.7, 4.5) * mm, "end": v(7.7, -0.5) * mm});
            skLineSegment(sketch, "E228", {"start": v(32.7, 4.5) * mm, "end": v(32.7, -0.5) * mm});
            skLineSegment(sketch, "E229", {"start": v(55.2, 4.5) * mm, "end": v(55.2, -0.5) * mm});
            skLineSegment(sketch, "E230", {"start": v(77.7, 4.5) * mm, "end": v(77.7, -0.5) * mm});
            skLineSegment(sketch, "E231", {"start": v(102.7, 4.5) * mm, "end": v(102.7, -0.5) * mm});
            skSolve(sketch);
        }
        {
            var Q0;
            {var subQ0=sQuery(id+"F25.wireOp",EDGE,"E212");Q0=makeQuery(id+"F25.imprint","IMPRINT",FACE,{"disambiguationData":[TD([[makeQuery(id+"F25.imprint","IMPRINT",EDGE,{"derivedFrom":subQ0}),1.0]])]});}
            var Q1;
            {var subQ0=sQuery(id+"F25.wireOp",EDGE,"E214");Q1=makeQuery(id+"F25.imprint","IMPRINT",FACE,{"disambiguationData":[TD([[makeQuery(id+"F25.imprint","IMPRINT",EDGE,{"derivedFrom":subQ0}),1.0]])]});}
            var Q2;
            {var subQ0=sQuery(id+"F25.wireOp",EDGE,"E216");Q2=makeQuery(id+"F25.imprint","IMPRINT",FACE,{"disambiguationData":[TD([[makeQuery(id+"F25.imprint","IMPRINT",EDGE,{"derivedFrom":subQ0}),1.0]])]});}
            var Q3;
            {var subQ0=sQuery(id+"F25.wireOp",EDGE,"E218");Q3=makeQuery(id+"F25.imprint","IMPRINT",FACE,{"disambiguationData":[TD([[makeQuery(id+"F25.imprint","IMPRINT",EDGE,{"derivedFrom":subQ0}),1.0]])]});}
            var Q4;
            {var subQ0=sQuery(id+"F25.wireOp",EDGE,"E220");Q4=makeQuery(id+"F25.imprint","IMPRINT",FACE,{"disambiguationData":[TD([[makeQuery(id+"F25.imprint","IMPRINT",EDGE,{"derivedFrom":subQ0}),1.0]])]});}
            var Q5;
            {var subQ0=sQuery(id+"F25.wireOp",EDGE,"E222");Q5=makeQuery(id+"F25.imprint","IMPRINT",FACE,{"disambiguationData":[TD([[makeQuery(id+"F25.imprint","IMPRINT",EDGE,{"derivedFrom":subQ0}),1.0]])]});}
            extrude(context, id + "F26", {"entities" : qUnion([Q0, Q1, Q2, Q3, Q4, Q5]), "operationType" : NewBodyOperationType.ADD, "oppositeDirection" : true, "depth" : 30 * mm, "offsetDistance" : 25 * mm});
        }
        {
            var Q0;
            Q0=makeQuery(id+"F1.opExtrude","CAP_FACE",FACE,{"disambiguationData":[OSD([sQuery(id+"F0.wireOp",EDGE,"E0"),sQuery(id+"F0.wireOp",EDGE,"E1.0.1.0"),sQuery(id+"F0.wireOp",EDGE,"E1.1.0.0"),sQuery(id+"F0.wireOp",EDGE,"E1.1.1.0"),sQuery(id+"F0.wireOp",EDGE,"E2"),sQuery(id+"F0.wireOp",EDGE,"E3.0.1.0"),sQuery(id+"F0.wireOp",EDGE,"E3.1.0.0"),sQuery(id+"F0.wireOp",EDGE,"E3.1.1.0"),sQuery(id+"F0.wireOp",EDGE,"E4"),sQuery(id+"F0.wireOp",EDGE,"E5.0.1.0"),sQuery(id+"F0.wireOp",EDGE,"E5.0.2.0"),sQuery(id+"F0.wireOp",EDGE,"E5.1.0.0"),sQuery(id+"F0.wireOp",EDGE,"E5.1.1.0"),sQuery(id+"F0.wireOp",EDGE,"E5.1.2.0"),sQuery(id+"F0.wireOp",EDGE,"E5.2.0.0"),sQuery(id+"F0.wireOp",EDGE,"E5.2.1.0"),sQuery(id+"F0.wireOp",EDGE,"E5.2.2.0"),sQuery(id+"F0.wireOp",EDGE,"E6"),sQuery(id+"F0.wireOp",EDGE,"E7.1.0.0"),sQuery(id+"F0.wireOp",EDGE,"E7.2.0.0"),sQuery(id+"F0.wireOp",EDGE,"E7.3.0.0"),sQuery(id+"F0.wireOp",EDGE,"E7.4.0.0"),sQuery(id+"F0.wireOp",EDGE,"E7.5.0.0"),sQuery(id+"F0.wireOp",EDGE,"E8.0.6.0"),sQuery(id+"F0.wireOp",EDGE,"E8.0.7.0"),sQuery(id+"F0.wireOp",EDGE,"E8.0.8.0"),sQuery(id+"F0.wireOp",EDGE,"E8.0.9.0"),sQuery(id+"F0.wireOp",EDGE,"E9.0.10.0"),sQuery(id+"F0.wireOp",EDGE,"E10.1.0.0"),sQuery(id+"F0.wireOp",EDGE,"E10.2.0.0"),sQuery(id+"F0.wireOp",EDGE,"E13"),sQuery(id+"F0.wireOp",EDGE,"E14"),sQuery(id+"F0.wireOp",EDGE,"E15"),sQuery(id+"F0.wireOp",EDGE,"E17"),sQuery(id+"F0.wireOp",EDGE,"E18"),sQuery(id+"F0.wireOp",EDGE,"E19"),sQuery(id+"F0.wireOp",EDGE,"E20"),sQuery(id+"F0.wireOp",EDGE,"E21"),sQuery(id+"F0.wireOp",EDGE,"E22"),sQuery(id+"F0.wireOp",EDGE,"E23.1.0.0"),sQuery(id+"F0.wireOp",EDGE,"E23.2.0.0"),sQuery(id+"F0.wireOp",EDGE,"E23.3.0.0")])],"isStart":false});
            var sketch = newSketch(context, id + "F27", { "sketchPlane" : qUnion([Q0])});
            skLineSegment(sketch, "E232.0", {"start": v(126.2, 15.35) * mm, "end": v(-24.8, 15.35) * mm});
            skArc(sketch, "E232.1", {"start": v(-24.8, 21.2) * mm, "mid": v(-19.8, 20.35) * mm, "end": v(-14.8, 21.2) * mm});
            skPoint(sketch, "E232.2", {"position": v(-14.8, 18.08) * mm});
            skPoint(sketch, "E232.3", {"position": v(-24.8, 18.08) * mm});
            skLineSegment(sketch, "E233", {"start": v(-24.8, 18.08) * mm, "end": v(-24.8, 21.2) * mm});
            skLineSegment(sketch, "E234", {"start": v(-24.8, 18.08) * mm, "end": v(-24.8, 15.35) * mm});
            skLineSegment(sketch, "E235", {"start": v(-14.8, 18.08) * mm, "end": v(-14.8, 21.2) * mm});
            skLineSegment(sketch, "E236", {"start": v(-14.8, 18.08) * mm, "end": v(-14.8, 15.35) * mm});
            skPoint(sketch, "E237.orphan", {"position": v(-45.8, 15.35) * mm});
            skCircle(sketch, "E238.0", {"center": v(7.7, 34.04) * mm, "radius": 8.5 * mm});
            skCircle(sketch, "E238.1", {"center": v(32.7, 32.85) * mm, "radius": 12.5 * mm});
            skCircle(sketch, "E238.2", {"center": v(55.2, 32.85) * mm, "radius": 6 * mm});
            skCircle(sketch, "E238.3", {"center": v(77.7, 32.85) * mm, "radius": 12.5 * mm});
            skCircle(sketch, "E238.4", {"center": v(102.7, 32.85) * mm, "radius": 8.5 * mm});
            skPoint(sketch, "E238.5", {"position": v(97.7, 20.47) * mm});
            skPoint(sketch, "E238.6", {"position": v(107.7, 20.47) * mm});
            skPoint(sketch, "E238.7", {"position": v(82.7, 18.17) * mm});
            skPoint(sketch, "E238.8", {"position": v(72.7, 18.17) * mm});
            skPoint(sketch, "E238.9", {"position": v(60.2, 22.28) * mm});
            skPoint(sketch, "E238.10", {"position": v(50.2, 22.28) * mm});
            skPoint(sketch, "E238.11", {"position": v(37.7, 18.17) * mm});
            skPoint(sketch, "E238.12", {"position": v(27.7, 18.17) * mm});
            skPoint(sketch, "E238.13", {"position": v(12.7, 21.07) * mm});
            skPoint(sketch, "E238.14", {"position": v(2.7, 21.07) * mm});
            skLineSegment(sketch, "E239", {"start": v(2.7, 15.35) * mm, "end": v(2.7, 27.16) * mm});
            skLineSegment(sketch, "E240", {"start": v(12.7, 15.35) * mm, "end": v(12.7, 27.16) * mm});
            skLineSegment(sketch, "E241", {"start": v(27.7, 15.35) * mm, "end": v(27.7, 21.39) * mm});
            skLineSegment(sketch, "E242", {"start": v(37.7, 15.35) * mm, "end": v(37.7, 21.39) * mm});
            skLineSegment(sketch, "E243", {"start": v(72.7, 15.35) * mm, "end": v(72.7, 21.39) * mm});
            skLineSegment(sketch, "E244", {"start": v(82.7, 15.35) * mm, "end": v(82.7, 21.39) * mm});
            skLineSegment(sketch, "E245", {"start": v(97.7, 15.35) * mm, "end": v(97.7, 25.97) * mm});
            skLineSegment(sketch, "E246", {"start": v(107.7, 15.35) * mm, "end": v(107.7, 25.97) * mm});
            skLineSegment(sketch, "E247", {"start": v(50.2, 15.35) * mm, "end": v(50.2, 29.53) * mm});
            skLineSegment(sketch, "E248", {"start": v(60.2, 15.35) * mm, "end": v(60.2, 29.53) * mm});
            skSolve(sketch);
        }
        {
            var Q0;
            Q0=makeQuery(id+"F27.imprint","IMPRINT",FACE,{"disambiguationData":[TD([[makeQuery(id+"F27.imprint","IMPRINT",EDGE,{"derivedFrom":sQuery(id+"F27.wireOp",EDGE,"E232.1")}),-1.0]])]});
            var Q1;
            {var subQ0=sQuery(id+"F27.wireOp",EDGE,"E239");Q1=makeQuery(id+"F27.imprint","IMPRINT",FACE,{"disambiguationData":[TD([[makeQuery(id+"F27.imprint","IMPRINT",EDGE,{"derivedFrom":subQ0}),-1.0]])]});}
            var Q2;
            {var subQ0=sQuery(id+"F27.wireOp",EDGE,"E241");Q2=makeQuery(id+"F27.imprint","IMPRINT",FACE,{"disambiguationData":[TD([[makeQuery(id+"F27.imprint","IMPRINT",EDGE,{"derivedFrom":subQ0}),-1.0]])]});}
            var Q3;
            {var subQ0=sQuery(id+"F27.wireOp",EDGE,"E243");Q3=makeQuery(id+"F27.imprint","IMPRINT",FACE,{"disambiguationData":[TD([[makeQuery(id+"F27.imprint","IMPRINT",EDGE,{"derivedFrom":subQ0}),-1.0]])]});}
            var Q4;
            {var subQ0=sQuery(id+"F27.wireOp",EDGE,"E245");Q4=makeQuery(id+"F27.imprint","IMPRINT",FACE,{"disambiguationData":[TD([[makeQuery(id+"F27.imprint","IMPRINT",EDGE,{"derivedFrom":subQ0}),-1.0]])]});}
            var Q5;
            {var subQ0=sQuery(id+"F27.wireOp",EDGE,"E247");Q5=makeQuery(id+"F27.imprint","IMPRINT",FACE,{"disambiguationData":[TD([[makeQuery(id+"F27.imprint","IMPRINT",EDGE,{"derivedFrom":subQ0}),-1.0]])]});}
            var Q6;
            Q6=makeQuery(id+"F1.opExtrude","CAP_FACE",FACE,{"disambiguationData":[OSD([sQuery(id+"F0.wireOp",EDGE,"E0"),sQuery(id+"F0.wireOp",EDGE,"E1.0.1.0"),sQuery(id+"F0.wireOp",EDGE,"E1.1.0.0"),sQuery(id+"F0.wireOp",EDGE,"E1.1.1.0"),sQuery(id+"F0.wireOp",EDGE,"E2"),sQuery(id+"F0.wireOp",EDGE,"E3.0.1.0"),sQuery(id+"F0.wireOp",EDGE,"E3.1.0.0"),sQuery(id+"F0.wireOp",EDGE,"E3.1.1.0"),sQuery(id+"F0.wireOp",EDGE,"E4"),sQuery(id+"F0.wireOp",EDGE,"E5.0.1.0"),sQuery(id+"F0.wireOp",EDGE,"E5.0.2.0"),sQuery(id+"F0.wireOp",EDGE,"E5.1.0.0"),sQuery(id+"F0.wireOp",EDGE,"E5.1.1.0"),sQuery(id+"F0.wireOp",EDGE,"E5.1.2.0"),sQuery(id+"F0.wireOp",EDGE,"E5.2.0.0"),sQuery(id+"F0.wireOp",EDGE,"E5.2.1.0"),sQuery(id+"F0.wireOp",EDGE,"E5.2.2.0"),sQuery(id+"F0.wireOp",EDGE,"E6"),sQuery(id+"F0.wireOp",EDGE,"E7.1.0.0"),sQuery(id+"F0.wireOp",EDGE,"E7.2.0.0"),sQuery(id+"F0.wireOp",EDGE,"E7.3.0.0"),sQuery(id+"F0.wireOp",EDGE,"E7.4.0.0"),sQuery(id+"F0.wireOp",EDGE,"E7.5.0.0"),sQuery(id+"F0.wireOp",EDGE,"E8.0.6.0"),sQuery(id+"F0.wireOp",EDGE,"E8.0.7.0"),sQuery(id+"F0.wireOp",EDGE,"E8.0.8.0"),sQuery(id+"F0.wireOp",EDGE,"E8.0.9.0"),sQuery(id+"F0.wireOp",EDGE,"E9.0.10.0"),sQuery(id+"F0.wireOp",EDGE,"E10.1.0.0"),sQuery(id+"F0.wireOp",EDGE,"E10.2.0.0"),sQuery(id+"F0.wireOp",EDGE,"E13"),sQuery(id+"F0.wireOp",EDGE,"E14"),sQuery(id+"F0.wireOp",EDGE,"E15"),sQuery(id+"F0.wireOp",EDGE,"E17"),sQuery(id+"F0.wireOp",EDGE,"E18"),sQuery(id+"F0.wireOp",EDGE,"E19"),sQuery(id+"F0.wireOp",EDGE,"E20"),sQuery(id+"F0.wireOp",EDGE,"E21"),sQuery(id+"F0.wireOp",EDGE,"E22"),sQuery(id+"F0.wireOp",EDGE,"E23.1.0.0"),sQuery(id+"F0.wireOp",EDGE,"E23.2.0.0"),sQuery(id+"F0.wireOp",EDGE,"E23.3.0.0")])],"isStart":false});
            extrude(context, id + "F28", {"entities" : qUnion([Q0, Q1, Q2, Q3, Q4, Q5]), "operationType" : NewBodyOperationType.REMOVE, "depth" : 25 * mm, "endBoundEntityFace" : qUnion([Q6]), "offsetDistance" : 25 * mm});
        }
        {
            var Q0;
            {var subQ0=sQuery(id+"F25.wireOp",EDGE,"E225.left");Q0=makeQuery(id+"F25.imprint","IMPRINT",FACE,{"disambiguationData":[TD([[makeQuery(id+"F25.imprint","IMPRINT",EDGE,{"derivedFrom":subQ0}),1.0]])]});}
            var Q1;
            {var subQ0=sQuery(id+"F25.wireOp",EDGE,"E227");Q1=makeQuery(id+"F25.imprint","IMPRINT",FACE,{"disambiguationData":[TD([[makeQuery(id+"F25.imprint","IMPRINT",EDGE,{"derivedFrom":subQ0}),1.0]])]});}
            var Q2;
            {var subQ0=sQuery(id+"F25.wireOp",EDGE,"E229");Q2=makeQuery(id+"F25.imprint","IMPRINT",FACE,{"disambiguationData":[TD([[makeQuery(id+"F25.imprint","IMPRINT",EDGE,{"derivedFrom":subQ0}),1.0]])]});}
            var Q3;
            {var subQ0=sQuery(id+"F25.wireOp",EDGE,"E225.right");Q3=makeQuery(id+"F25.imprint","IMPRINT",FACE,{"disambiguationData":[TD([[makeQuery(id+"F25.imprint","IMPRINT",EDGE,{"derivedFrom":subQ0}),-1.0]])]});}
            extrude(context, id + "F29", {"entities" : qUnion([Q0, Q1, Q2, Q3]), "operationType" : NewBodyOperationType.REMOVE, "oppositeDirection" : true, "depth" : 8 * mm, "offsetDistance" : 25 * mm});
        }
    });
